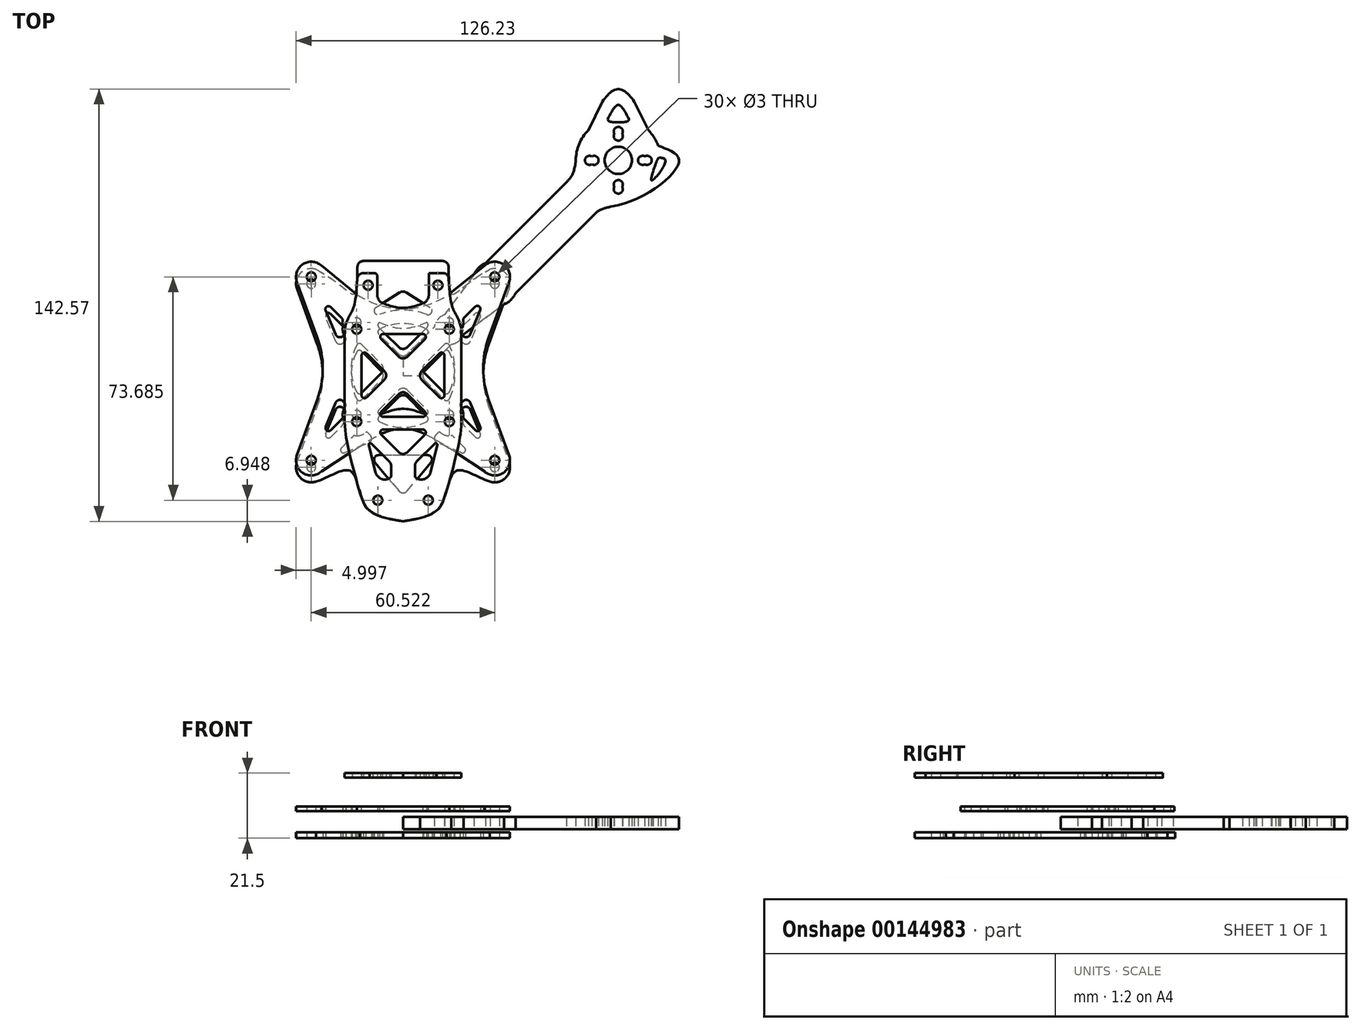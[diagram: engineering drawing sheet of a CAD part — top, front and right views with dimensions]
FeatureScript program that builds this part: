
annotation { "Feature Type Name" : "Feature", "Feature Type Description" : "" }
export const myFeature = defineFeature(function(context is Context, id is Id, definition is map)
    precondition{}
    {
        {
            var Q0;
            Q0=qCreatedBy(makeId("Top.planeOp"),FACE);
            var sketch = newSketch(context, id + "F0", { "sketchPlane" : qUnion([Q0])});
            skLineSegment(sketch, "E0.bottom", {"start": v(-15.25, 15.25) * mm, "end": v(15.25, 15.25) * mm, "construction": true});
            skLineSegment(sketch, "E0.top", {"start": v(-15.25, -15.25) * mm, "end": v(15.25, -15.25) * mm, "construction": true});
            skLineSegment(sketch, "E0.left", {"start": v(-15.25, 15.25) * mm, "end": v(-15.25, -15.25) * mm, "construction": true});
            skLineSegment(sketch, "E0.right", {"start": v(15.25, 15.25) * mm, "end": v(15.25, -15.25) * mm, "construction": true});
            skPoint(sketch, "E0.middle", {"position": v(0, 0) * mm});
            skLineSegment(sketch, "E1.bottom", {"start": v(30.25, 30.25) * mm, "end": v(-30.25, 30.25) * mm, "construction": true});
            skLineSegment(sketch, "E1.top", {"start": v(30.25, -30.25) * mm, "end": v(-30.25, -30.25) * mm, "construction": true});
            skLineSegment(sketch, "E1.left", {"start": v(30.25, 30.25) * mm, "end": v(30.25, -30.25) * mm, "construction": true});
            skLineSegment(sketch, "E1.right", {"start": v(-30.25, 30.25) * mm, "end": v(-30.25, -30.25) * mm, "construction": true});
            skLineSegment(sketch, "E2.bottom", {"start": v(-70.96, 70.96) * mm, "end": v(70.96, 70.96) * mm, "construction": true});
            skLineSegment(sketch, "E2.top", {"start": v(-70.96, -70.96) * mm, "end": v(70.96, -70.96) * mm, "construction": true});
            skLineSegment(sketch, "E2.left", {"start": v(-70.96, 70.96) * mm, "end": v(-70.96, -70.96) * mm, "construction": true});
            skLineSegment(sketch, "E2.right", {"start": v(70.96, 70.96) * mm, "end": v(70.96, -70.96) * mm, "construction": true});
            skCircle(sketch, "E3", {"center": v(70.96, 70.96) * mm, "radius": 8 * mm, "construction": true});
            skCircle(sketch, "E4", {"center": v(70.96, -70.96) * mm, "radius": 8 * mm, "construction": true});
            skCircle(sketch, "E5", {"center": v(-70.96, -70.96) * mm, "radius": 8 * mm, "construction": true});
            skCircle(sketch, "E6", {"center": v(-70.96, 70.96) * mm, "radius": 8 * mm, "construction": true});
            skCircle(sketch, "E7", {"center": v(70.96, 70.96) * mm, "radius": 9.5 * mm, "construction": true});
            skCircle(sketch, "E8", {"center": v(70.96, -70.96) * mm, "radius": 9.5 * mm, "construction": true});
            skCircle(sketch, "E9", {"center": v(-70.96, -70.96) * mm, "radius": 9.5 * mm, "construction": true});
            skCircle(sketch, "E10", {"center": v(-70.96, 70.96) * mm, "radius": 9.5 * mm, "construction": true});
            skCircle(sketch, "E11", {"center": v(70.96, 70.96) * mm, "radius": 14 * mm, "construction": true});
            skCircle(sketch, "E12", {"center": v(-70.96, 70.96) * mm, "radius": 14 * mm, "construction": true});
            skCircle(sketch, "E13", {"center": v(70.96, -70.96) * mm, "radius": 14 * mm, "construction": true});
            skCircle(sketch, "E14", {"center": v(-70.96, -70.96) * mm, "radius": 14 * mm, "construction": true});
            skCircle(sketch, "E15", {"center": v(70.96, 70.96) * mm, "radius": 63.5 * mm, "construction": true});
            skCircle(sketch, "E16", {"center": v(70.96, -70.96) * mm, "radius": 63.5 * mm, "construction": true});
            skCircle(sketch, "E17", {"center": v(-70.96, -70.96) * mm, "radius": 63.5 * mm, "construction": true});
            skCircle(sketch, "E18", {"center": v(-70.96, 70.96) * mm, "radius": 63.5 * mm, "construction": true});
            skLineSegment(sketch, "E19", {"start": v(0, 30.25) * mm, "end": v(0, 37.76) * mm, "construction": true});
            skLineSegment(sketch, "E20", {"start": v(0, 37.76) * mm, "end": v(-15, 37.76) * mm, "construction": true});
            skLineSegment(sketch, "E21", {"start": v(0, 37.76) * mm, "end": v(15, 37.76) * mm, "construction": true});
            skLineSegment(sketch, "E22", {"start": v(0, -30.25) * mm, "end": v(0, -37.76) * mm, "construction": true});
            skLineSegment(sketch, "E23.bottom", {"start": v(-26.17, 26.25) * mm, "end": v(26.21, 26.25) * mm, "construction": true});
            skLineSegment(sketch, "E23.top", {"start": v(-26.21, -26.25) * mm, "end": v(26.17, -26.25) * mm, "construction": true});
            skLineSegment(sketch, "E23.left", {"start": v(-26.17, 26.25) * mm, "end": v(-26.17, -26.13) * mm, "construction": true});
            skLineSegment(sketch, "E23.right", {"start": v(26.21, 26.25) * mm, "end": v(26.21, -26.2) * mm, "construction": true});
            skCircle(sketch, "E24", {"center": v(30.25, 30.25) * mm, "radius": 5 * mm, "construction": true});
            skCircle(sketch, "E25", {"center": v(-30.25, 30.25) * mm, "radius": 5 * mm, "construction": true});
            skCircle(sketch, "E26", {"center": v(30.25, -30.25) * mm, "radius": 5 * mm, "construction": true});
            skCircle(sketch, "E27", {"center": v(-30.25, -30.25) * mm, "radius": 5 * mm, "construction": true});
            skLineSegment(sketch, "E28.bottom", {"start": v(24.5, 24.5) * mm, "end": v(-24.5, 24.5) * mm, "construction": true});
            skLineSegment(sketch, "E28.top", {"start": v(24.5, -24.5) * mm, "end": v(-24.5, -24.5) * mm, "construction": true});
            skLineSegment(sketch, "E28.left", {"start": v(24.5, 24.5) * mm, "end": v(24.5, -24.5) * mm, "construction": true});
            skLineSegment(sketch, "E28.right", {"start": v(-24.5, 24.5) * mm, "end": v(-24.5, -24.5) * mm, "construction": true});
            skLineSegment(sketch, "E29", {"start": v(-26.17, 26.25) * mm, "end": v(-30.25, 30.25) * mm, "construction": true});
            skLineSegment(sketch, "E30", {"start": v(-26.68, 26.75) * mm, "end": v(-33.82, 33.75) * mm, "construction": true});
            skLineSegment(sketch, "E31", {"start": v(-31.8, 31.77) * mm, "end": v(-28.66, 34.99) * mm, "construction": true});
            skLineSegment(sketch, "E32", {"start": v(-31.8, 31.77) * mm, "end": v(-34.96, 28.56) * mm, "construction": true});
            skArc(sketch, "E33", {"start": v(-28.66, 34.99) * mm, "mid": v(-33.82, 33.75) * mm, "end": v(-34.96, 28.56) * mm});
            skLineSegment(sketch, "E34", {"start": v(26.21, 26.25) * mm, "end": v(30.25, 30.25) * mm, "construction": true});
            skLineSegment(sketch, "E35", {"start": v(26.7, 26.73) * mm, "end": v(33.8, 33.77) * mm, "construction": true});
            skLineSegment(sketch, "E36", {"start": v(31.8, 31.78) * mm, "end": v(34.96, 28.58) * mm, "construction": true});
            skLineSegment(sketch, "E37", {"start": v(31.8, 31.78) * mm, "end": v(28.63, 34.98) * mm, "construction": true});
            skArc(sketch, "E38", {"start": v(34.96, 28.58) * mm, "mid": v(33.8, 33.77) * mm, "end": v(28.63, 34.98) * mm});
            skLineSegment(sketch, "E39", {"start": v(26.17, -26.25) * mm, "end": v(30.25, -30.25) * mm, "construction": true});
            skLineSegment(sketch, "E40", {"start": v(26.68, -26.75) * mm, "end": v(33.82, -33.75) * mm, "construction": true});
            skLineSegment(sketch, "E41", {"start": v(31.8, -31.77) * mm, "end": v(34.96, -28.56) * mm, "construction": true});
            skLineSegment(sketch, "E42", {"start": v(31.8, -31.77) * mm, "end": v(28.66, -34.99) * mm, "construction": true});
            skArc(sketch, "E43", {"start": v(28.66, -34.99) * mm, "mid": v(33.82, -33.75) * mm, "end": v(34.96, -28.56) * mm});
            skLineSegment(sketch, "E44", {"start": v(-26.21, -26.25) * mm, "end": v(-30.25, -30.25) * mm, "construction": true});
            skLineSegment(sketch, "E45", {"start": v(-26.7, -26.73) * mm, "end": v(-33.8, -33.77) * mm, "construction": true});
            skLineSegment(sketch, "E46", {"start": v(-31.8, -31.78) * mm, "end": v(-28.63, -34.98) * mm, "construction": true});
            skLineSegment(sketch, "E47", {"start": v(-31.8, -31.78) * mm, "end": v(-34.96, -28.58) * mm, "construction": true});
            skArc(sketch, "E48", {"start": v(-34.96, -28.58) * mm, "mid": v(-33.8, -33.77) * mm, "end": v(-28.63, -34.98) * mm});
            skLineSegment(sketch, "E49", {"start": v(-34.96, -28.58) * mm, "end": v(-28.28, -10.31) * mm});
            skLineSegment(sketch, "E50", {"start": v(-28.28, 10.31) * mm, "end": v(-34.96, 28.56) * mm});
            skLineSegment(sketch, "E51", {"start": v(34.96, 28.58) * mm, "end": v(28.28, 10.31) * mm});
            skLineSegment(sketch, "E52", {"start": v(28.28, -10.31) * mm, "end": v(34.96, -28.56) * mm});
            skPoint(sketch, "E53.visualSharp", {"position": v(24.5, 0) * mm});
            skArc(sketch, "E53.filletArc", {"start": v(28.28, 10.31) * mm, "mid": v(26.45, 0) * mm, "end": v(28.28, -10.31) * mm});
            skPoint(sketch, "E54.visualSharp", {"position": v(-24.5, 0) * mm});
            skArc(sketch, "E54.filletArc", {"start": v(-28.28, -10.31) * mm, "mid": v(-26.45, 0) * mm, "end": v(-28.28, 10.31) * mm});
            skFitSpline(sketch, "E55", {"points": [v(-28.66, 34.99) * mm, v(-15, 37.76) * mm], "startDerivative": vector(40.9, -21.49) * mm, "endDerivative": vector(0.75, 54.16) * mm});
            skFitSpline(sketch, "E56", {"points": [v(15, 37.76) * mm, v(28.63, 34.98) * mm], "startDerivative": vector(0.75, -54.16) * mm, "endDerivative": vector(40.9, 21.46) * mm});
            skLineSegment(sketch, "E57", {"start": v(-15.25, 19.7) * mm, "end": v(15.25, 19.7) * mm, "construction": true});
            skPoint(sketch, "E58.endSnap0", {"position": v(0, -15.25) * mm});
            skLineSegment(sketch, "E59", {"start": v(-15.25, -19.7) * mm, "end": v(15.25, -19.7) * mm, "construction": true});
            skLineSegment(sketch, "E60", {"start": v(-14.33, -37.76) * mm, "end": v(14.33, -37.76) * mm, "construction": true});
            skLineSegment(sketch, "E61", {"start": v(-13.03, 37.76) * mm, "end": v(13.03, 37.76) * mm});
            skCircle(sketch, "E62", {"center": v(-30.25, 30.25) * mm, "radius": 1.5 * mm});
            skCircle(sketch, "E63", {"center": v(30.25, 30.25) * mm, "radius": 1.5 * mm});
            skCircle(sketch, "E64", {"center": v(15.25, 15.25) * mm, "radius": 1.5 * mm});
            skCircle(sketch, "E65", {"center": v(-15.25, 15.25) * mm, "radius": 1.5 * mm});
            skCircle(sketch, "E66", {"center": v(-15.25, -15.25) * mm, "radius": 1.5 * mm});
            skCircle(sketch, "E67", {"center": v(15.25, -15.25) * mm, "radius": 1.5 * mm});
            skCircle(sketch, "E68", {"center": v(30.25, -30.25) * mm, "radius": 1.5 * mm});
            skCircle(sketch, "E69", {"center": v(-30.25, -30.25) * mm, "radius": 1.5 * mm});
            skLineSegment(sketch, "E70", {"start": v(15, 37.76) * mm, "end": v(11.5, 37.76) * mm, "construction": true});
            skLineSegment(sketch, "E71", {"start": v(-15, 37.76) * mm, "end": v(-11.5, 37.76) * mm, "construction": true});
            skLineSegment(sketch, "E72", {"start": v(11.5, 37.76) * mm, "end": v(11.5, 29.76) * mm, "construction": true});
            skLineSegment(sketch, "E73", {"start": v(-11.5, 37.76) * mm, "end": v(-11.5, 29.76) * mm, "construction": true});
            skCircle(sketch, "E74", {"center": v(-11.5, 29.76) * mm, "radius": 1.5 * mm});
            skCircle(sketch, "E75", {"center": v(11.5, 29.76) * mm, "radius": 1.5 * mm});
            skLineSegment(sketch, "E76", {"start": v(0, 37.76) * mm, "end": v(0, 15.25) * mm, "construction": true});
            skLineSegment(sketch, "E77", {"start": v(0, -44.58) * mm, "end": v(-11, -44.58) * mm, "construction": true});
            skLineSegment(sketch, "E78", {"start": v(0, -44.58) * mm, "end": v(11, -44.58) * mm, "construction": true});
            skPoint(sketch, "E79.visualSharp", {"position": v(-14.33, -37.76) * mm});
            skPoint(sketch, "E80.visualSharp", {"position": v(14.33, -37.76) * mm});
            skCircle(sketch, "E81", {"center": v(0, 0) * mm, "radius": 17.11 * mm, "construction": true});
            skLineSegment(sketch, "E82", {"start": v(0, 0) * mm, "end": v(14.1, 14.1) * mm, "construction": true});
            skLineSegment(sketch, "E83", {"start": v(0, 0) * mm, "end": v(-15.25, 15.25) * mm, "construction": true});
            skLineSegment(sketch, "E84", {"start": v(0, 0) * mm, "end": v(-15.32, -15.32) * mm, "construction": true});
            skLineSegment(sketch, "E85", {"start": v(0, 0) * mm, "end": v(15.25, -15.25) * mm, "construction": true});
            skLineSegment(sketch, "E86", {"start": v(-10.7, 10.7) * mm, "end": v(-7.86, 13.52) * mm, "construction": true});
            skLineSegment(sketch, "E87", {"start": v(-10.7, 10.7) * mm, "end": v(-13.52, 7.86) * mm, "construction": true});
            skLineSegment(sketch, "E88", {"start": v(9.03, 9.03) * mm, "end": v(11.86, 6.2) * mm, "construction": true});
            skLineSegment(sketch, "E89", {"start": v(9.03, 9.03) * mm, "end": v(6.2, 11.86) * mm, "construction": true});
            skLineSegment(sketch, "E90", {"start": v(9.8, -9.8) * mm, "end": v(12.64, -6.98) * mm, "construction": true});
            skLineSegment(sketch, "E91", {"start": v(9.8, -9.8) * mm, "end": v(6.98, -12.64) * mm, "construction": true});
            skLineSegment(sketch, "E92", {"start": v(-9.52, -9.52) * mm, "end": v(-6.7, -12.35) * mm, "construction": true});
            skLineSegment(sketch, "E93", {"start": v(-9.52, -9.52) * mm, "end": v(-12.35, -6.7) * mm, "construction": true});
            skLineSegment(sketch, "E94.bottom", {"start": v(6.35, 6.35) * mm, "end": v(-6.35, 6.35) * mm, "construction": true});
            skLineSegment(sketch, "E94.top", {"start": v(6.35, -6.35) * mm, "end": v(-6.35, -6.35) * mm, "construction": true});
            skLineSegment(sketch, "E94.left", {"start": v(6.35, 6.35) * mm, "end": v(6.35, -6.35) * mm, "construction": true});
            skLineSegment(sketch, "E94.right", {"start": v(-6.35, 6.35) * mm, "end": v(-6.35, -6.35) * mm, "construction": true});
            skLineSegment(sketch, "E95", {"start": v(6.2, 11.86) * mm, "end": v(8.94, 14.6) * mm, "construction": true});
            skLineSegment(sketch, "E96", {"start": v(11.86, 6.2) * mm, "end": v(14.6, 8.94) * mm, "construction": true});
            skLineSegment(sketch, "E97", {"start": v(8, 13.66) * mm, "end": v(1.41, 7.07) * mm});
            skLineSegment(sketch, "E98", {"start": v(-1.41, 7.07) * mm, "end": v(-8, 13.66) * mm});
            skLineSegment(sketch, "E99", {"start": v(-13.52, 7.86) * mm, "end": v(-14.6, 8.94) * mm, "construction": true});
            skLineSegment(sketch, "E100", {"start": v(-6.7, -12.35) * mm, "end": v(-8.94, -14.6) * mm, "construction": true});
            skLineSegment(sketch, "E101", {"start": v(-8, -13.66) * mm, "end": v(-1.41, -7.07) * mm});
            skLineSegment(sketch, "E102", {"start": v(1.41, -7.07) * mm, "end": v(8, -13.66) * mm});
            skLineSegment(sketch, "E103", {"start": v(13.66, 8) * mm, "end": v(7.07, 1.41) * mm});
            skLineSegment(sketch, "E104", {"start": v(7.07, -1.41) * mm, "end": v(13.66, -8) * mm});
            skPoint(sketch, "E105", {"position": v(-7.77, 15.25) * mm});
            skPoint(sketch, "E106", {"position": v(7.77, 15.25) * mm});
            skPoint(sketch, "E107", {"position": v(15.25, 7.77) * mm});
            skPoint(sketch, "E108", {"position": v(15.25, -7.77) * mm});
            skPoint(sketch, "E109", {"position": v(7.77, -15.25) * mm});
            skPoint(sketch, "E110", {"position": v(-7.77, -15.25) * mm});
            skPoint(sketch, "E111", {"position": v(-15.25, -7.77) * mm});
            skPoint(sketch, "E112", {"position": v(-15.25, 7.77) * mm});
            skLineSegment(sketch, "E113", {"start": v(-7.79, 15.24) * mm, "end": v(-7.77, 15.25) * mm});
            skLineSegment(sketch, "E114", {"start": v(7.79, 15.24) * mm, "end": v(7.77, 15.25) * mm});
            skLineSegment(sketch, "E115", {"start": v(15.24, 7.79) * mm, "end": v(15.25, 7.77) * mm});
            skLineSegment(sketch, "E116", {"start": v(15.24, -7.79) * mm, "end": v(15.25, -7.77) * mm});
            skLineSegment(sketch, "E117", {"start": v(7.79, -15.24) * mm, "end": v(7.77, -15.25) * mm});
            skLineSegment(sketch, "E118", {"start": v(-7.77, -15.25) * mm, "end": v(-7.79, -15.24) * mm});
            skLineSegment(sketch, "E119", {"start": v(-15.24, -7.79) * mm, "end": v(-15.25, -7.77) * mm});
            skLineSegment(sketch, "E120", {"start": v(-15.24, 7.79) * mm, "end": v(-15.25, 7.77) * mm});
            skPoint(sketch, "E121", {"position": v(0, 17.11) * mm});
            skPoint(sketch, "E122", {"position": v(17.11, 0) * mm});
            skPoint(sketch, "E123", {"position": v(-17.11, 0) * mm});
            skPoint(sketch, "E124", {"position": v(0, -17.11) * mm});
            skArc(sketch, "E125", {"start": v(7.77, 15.25) * mm, "mid": v(0, 17.11) * mm, "end": v(-7.77, 15.25) * mm});
            skArc(sketch, "E126", {"start": v(15.25, -7.77) * mm, "mid": v(17.11, 0) * mm, "end": v(15.25, 7.77) * mm});
            skArc(sketch, "E127", {"start": v(-7.77, -15.25) * mm, "mid": v(0, -17.11) * mm, "end": v(7.77, -15.25) * mm});
            skArc(sketch, "E128", {"start": v(-15.25, 7.77) * mm, "mid": v(-17.11, 0) * mm, "end": v(-15.25, -7.77) * mm});
            skPoint(sketch, "E129.visualSharp", {"position": v(-5.66, 0) * mm});
            skPoint(sketch, "E130.visualSharp", {"position": v(-14.6, 8.94) * mm});
            skArc(sketch, "E130.filletArc", {"start": v(-13.66, 8) * mm, "mid": v(-14.5, 8.29) * mm, "end": v(-15.24, 7.79) * mm});
            skPoint(sketch, "E131.visualSharp", {"position": v(-14.6, -8.94) * mm});
            skArc(sketch, "E131.filletArc", {"start": v(-15.24, -7.79) * mm, "mid": v(-14.5, -8.29) * mm, "end": v(-13.66, -8) * mm});
            skPoint(sketch, "E132.visualSharp", {"position": v(-8.94, 14.6) * mm});
            skArc(sketch, "E132.filletArc", {"start": v(-7.79, 15.24) * mm, "mid": v(-8.29, 14.5) * mm, "end": v(-8, 13.66) * mm});
            skPoint(sketch, "E133.visualSharp", {"position": v(8.94, 14.6) * mm});
            skArc(sketch, "E133.filletArc", {"start": v(8, 13.66) * mm, "mid": v(8.29, 14.5) * mm, "end": v(7.79, 15.24) * mm});
            skPoint(sketch, "E134.visualSharp", {"position": v(14.6, -8.94) * mm});
            skArc(sketch, "E134.filletArc", {"start": v(13.66, -8) * mm, "mid": v(14.5, -8.29) * mm, "end": v(15.24, -7.79) * mm});
            skPoint(sketch, "E135.visualSharp", {"position": v(14.6, 8.94) * mm});
            skArc(sketch, "E135.filletArc", {"start": v(15.24, 7.79) * mm, "mid": v(14.5, 8.29) * mm, "end": v(13.66, 8) * mm});
            skPoint(sketch, "E136.visualSharp", {"position": v(8.94, -14.6) * mm});
            skArc(sketch, "E136.filletArc", {"start": v(7.79, -15.24) * mm, "mid": v(8.29, -14.5) * mm, "end": v(8, -13.66) * mm});
            skPoint(sketch, "E137.visualSharp", {"position": v(-8.94, -14.6) * mm});
            skArc(sketch, "E137.filletArc", {"start": v(-8, -13.66) * mm, "mid": v(-8.29, -14.5) * mm, "end": v(-7.79, -15.24) * mm});
            skLineSegment(sketch, "E138", {"start": v(-13.66, 8) * mm, "end": v(-7.07, 1.41) * mm});
            skLineSegment(sketch, "E139", {"start": v(-13.66, -8) * mm, "end": v(-7.07, -1.41) * mm});
            skArc(sketch, "E140.filletArc", {"start": v(-7.07, -1.41) * mm, "mid": v(-6.49, 0) * mm, "end": v(-7.07, 1.41) * mm});
            skPoint(sketch, "E141.visualSharp", {"position": v(0, -5.66) * mm});
            skArc(sketch, "E141.filletArc", {"start": v(1.41, -7.07) * mm, "mid": v(0, -6.49) * mm, "end": v(-1.41, -7.07) * mm});
            skPoint(sketch, "E142.visualSharp", {"position": v(5.66, 0) * mm});
            skArc(sketch, "E142.filletArc", {"start": v(7.07, 1.41) * mm, "mid": v(6.49, 0) * mm, "end": v(7.07, -1.41) * mm});
            skPoint(sketch, "E143.visualSharp", {"position": v(0, 5.66) * mm});
            skArc(sketch, "E143.filletArc", {"start": v(-1.41, 7.07) * mm, "mid": v(0, 6.49) * mm, "end": v(1.41, 7.07) * mm});
            skLineSegment(sketch, "E144", {"start": v(-12.9, 12.9) * mm, "end": v(-11.14, 14.67) * mm, "construction": true});
            skLineSegment(sketch, "E145", {"start": v(-12.9, 12.9) * mm, "end": v(-14.67, 11.14) * mm, "construction": true});
            skLineSegment(sketch, "E146", {"start": v(-14.67, 11.14) * mm, "end": v(-27.4, 23.87) * mm, "construction": true});
            skPoint(sketch, "E147", {"position": v(-17.57, 14.03) * mm});
            skCircle(sketch, "E148", {"center": v(-15.25, 15.25) * mm, "radius": 4.62 * mm, "construction": true});
            skLineSegment(sketch, "E149", {"start": v(-27.4, 23.87) * mm, "end": v(-21.1, 8.64) * mm, "construction": true});
            skLineSegment(sketch, "E150", {"start": v(-15.25, 15.25) * mm, "end": v(-21.32, 9.18) * mm, "construction": true});
            skLineSegment(sketch, "E151", {"start": v(-18.86, 11.64) * mm, "end": v(-19.74, 10.76) * mm});
            skLineSegment(sketch, "E152", {"start": v(-22.18, 11.25) * mm, "end": v(-25.48, 19.23) * mm});
            skLineSegment(sketch, "E153", {"start": v(-23.85, 20.32) * mm, "end": v(-20.04, 16.5) * mm});
            skLineSegment(sketch, "E154", {"start": v(-19.83, 15.85) * mm, "end": v(-19.85, 15.74) * mm});
            skLineSegment(sketch, "E155", {"start": v(-18.84, 12.33) * mm, "end": v(-18.85, 12.35) * mm});
            skPoint(sketch, "E156", {"position": v(-19.67, 13.9) * mm});
            skArc(sketch, "E157", {"start": v(-19.85, 15.74) * mm, "mid": v(-19.69, 13.95) * mm, "end": v(-18.85, 12.35) * mm});
            skPoint(sketch, "E158.visualSharp", {"position": v(-27.4, 23.87) * mm});
            skArc(sketch, "E158.filletArc", {"start": v(-23.85, 20.32) * mm, "mid": v(-25.11, 20.44) * mm, "end": v(-25.48, 19.23) * mm});
            skPoint(sketch, "E159.visualSharp", {"position": v(-21.32, 9.18) * mm});
            skArc(sketch, "E159.filletArc", {"start": v(-22.18, 11.25) * mm, "mid": v(-21.1, 10.35) * mm, "end": v(-19.74, 10.76) * mm});
            skPoint(sketch, "E160.visualSharp", {"position": v(-18.52, 11.98) * mm});
            skArc(sketch, "E160.filletArc", {"start": v(-18.86, 11.64) * mm, "mid": v(-18.7, 11.98) * mm, "end": v(-18.84, 12.33) * mm});
            skPoint(sketch, "E161.visualSharp", {"position": v(-19.77, 16.23) * mm});
            skArc(sketch, "E161.filletArc", {"start": v(-19.83, 15.85) * mm, "mid": v(-19.86, 16.2) * mm, "end": v(-20.04, 16.5) * mm});
            skCircle(sketch, "E162", {"center": v(15.23, 15.26) * mm, "radius": 4.62 * mm, "construction": true});
            skLineSegment(sketch, "E163", {"start": v(15.23, 15.26) * mm, "end": v(12.9, 12.9) * mm, "construction": true});
            skLineSegment(sketch, "E164", {"start": v(12.9, 12.9) * mm, "end": v(14.68, 11.15) * mm, "construction": true});
            skLineSegment(sketch, "E165", {"start": v(12.9, 12.9) * mm, "end": v(11.12, 14.66) * mm, "construction": true});
            skLineSegment(sketch, "E166", {"start": v(11.12, 14.66) * mm, "end": v(23.85, 27.39) * mm, "construction": true});
            skLineSegment(sketch, "E167", {"start": v(14.68, 11.15) * mm, "end": v(27.32, 23.97) * mm, "construction": true});
            skLineSegment(sketch, "E168", {"start": v(15.25, 15.25) * mm, "end": v(21.37, 9.22) * mm, "construction": true});
            skLineSegment(sketch, "E169", {"start": v(21.37, 9.22) * mm, "end": v(27.32, 23.97) * mm, "construction": true});
            skLineSegment(sketch, "E170", {"start": v(19.8, 15.9) * mm, "end": v(19.82, 15.79) * mm});
            skLineSegment(sketch, "E171", {"start": v(18.84, 12.37) * mm, "end": v(18.86, 12.4) * mm});
            skLineSegment(sketch, "E172", {"start": v(20.01, 16.55) * mm, "end": v(23.8, 20.4) * mm});
            skLineSegment(sketch, "E173", {"start": v(25.45, 19.33) * mm, "end": v(22.2, 11.3) * mm});
            skLineSegment(sketch, "E174", {"start": v(19.77, 10.8) * mm, "end": v(18.86, 11.69) * mm});
            skPoint(sketch, "E175", {"position": v(19.65, 13.92) * mm});
            skArc(sketch, "E176", {"start": v(18.86, 12.4) * mm, "mid": v(19.68, 14) * mm, "end": v(19.82, 15.79) * mm});
            skPoint(sketch, "E177.visualSharp", {"position": v(18.53, 12.02) * mm});
            skArc(sketch, "E177.filletArc", {"start": v(18.84, 12.37) * mm, "mid": v(18.72, 12.03) * mm, "end": v(18.86, 11.69) * mm});
            skPoint(sketch, "E178.visualSharp", {"position": v(19.74, 16.28) * mm});
            skArc(sketch, "E178.filletArc", {"start": v(20.01, 16.55) * mm, "mid": v(19.83, 16.25) * mm, "end": v(19.8, 15.9) * mm});
            skPoint(sketch, "E179.visualSharp", {"position": v(27.32, 23.97) * mm});
            skArc(sketch, "E179.filletArc", {"start": v(25.45, 19.33) * mm, "mid": v(25.07, 20.54) * mm, "end": v(23.8, 20.4) * mm});
            skPoint(sketch, "E180.visualSharp", {"position": v(21.37, 9.22) * mm});
            skArc(sketch, "E180.filletArc", {"start": v(19.77, 10.8) * mm, "mid": v(21.12, 10.4) * mm, "end": v(22.2, 11.3) * mm});
            skCircle(sketch, "E181", {"center": v(-15.25, -15.25) * mm, "radius": 4.62 * mm, "construction": true});
            skCircle(sketch, "E182", {"center": v(15.25, -15.25) * mm, "radius": 4.62 * mm, "construction": true});
            skLineSegment(sketch, "E183", {"start": v(-15.25, -15.25) * mm, "end": v(-12.9, -12.9) * mm, "construction": true});
            skLineSegment(sketch, "E184", {"start": v(-12.9, -12.9) * mm, "end": v(-11.14, -14.67) * mm, "construction": true});
            skLineSegment(sketch, "E185", {"start": v(-12.9, -12.9) * mm, "end": v(-14.67, -11.14) * mm, "construction": true});
            skLineSegment(sketch, "E186", {"start": v(-11.14, -14.67) * mm, "end": v(-23.87, -27.4) * mm, "construction": true});
            skLineSegment(sketch, "E187", {"start": v(-14.67, -11.14) * mm, "end": v(-27.4, -23.87) * mm, "construction": true});
            skLineSegment(sketch, "E188", {"start": v(-15.25, -15.25) * mm, "end": v(-9.18, -21.32) * mm, "construction": true});
            skLineSegment(sketch, "E189", {"start": v(-15.25, -15.25) * mm, "end": v(-21.32, -9.18) * mm, "construction": true});
            skLineSegment(sketch, "E190", {"start": v(-25.48, -19.23) * mm, "end": v(-22.18, -11.25) * mm});
            skLineSegment(sketch, "E191", {"start": v(-19.74, -10.76) * mm, "end": v(-18.86, -11.64) * mm});
            skLineSegment(sketch, "E192", {"start": v(-23.85, -20.32) * mm, "end": v(-20.04, -16.5) * mm});
            skLineSegment(sketch, "E193", {"start": v(-18.84, -12.33) * mm, "end": v(-18.85, -12.35) * mm});
            skLineSegment(sketch, "E194", {"start": v(-19.83, -15.85) * mm, "end": v(-19.85, -15.74) * mm});
            skPoint(sketch, "E195", {"position": v(-19.69, -13.94) * mm});
            skArc(sketch, "E196", {"start": v(-18.85, -12.35) * mm, "mid": v(-19.69, -13.95) * mm, "end": v(-19.85, -15.74) * mm});
            skPoint(sketch, "E197.visualSharp", {"position": v(-18.52, -11.98) * mm});
            skArc(sketch, "E197.filletArc", {"start": v(-18.84, -12.33) * mm, "mid": v(-18.7, -11.98) * mm, "end": v(-18.86, -11.64) * mm});
            skPoint(sketch, "E198.visualSharp", {"position": v(-19.77, -16.23) * mm});
            skArc(sketch, "E198.filletArc", {"start": v(-20.04, -16.5) * mm, "mid": v(-19.86, -16.2) * mm, "end": v(-19.83, -15.85) * mm});
            skPoint(sketch, "E199.visualSharp", {"position": v(-27.4, -23.87) * mm});
            skArc(sketch, "E199.filletArc", {"start": v(-25.48, -19.23) * mm, "mid": v(-25.11, -20.44) * mm, "end": v(-23.85, -20.32) * mm});
            skPoint(sketch, "E200.visualSharp", {"position": v(-21.32, -9.18) * mm});
            skArc(sketch, "E200.filletArc", {"start": v(-19.74, -10.76) * mm, "mid": v(-21.1, -10.35) * mm, "end": v(-22.18, -11.25) * mm});
            skLineSegment(sketch, "E201", {"start": v(15.25, -15.25) * mm, "end": v(12.9, -12.9) * mm, "construction": true});
            skLineSegment(sketch, "E202", {"start": v(12.9, -12.9) * mm, "end": v(14.67, -11.14) * mm, "construction": true});
            skLineSegment(sketch, "E203", {"start": v(12.9, -12.9) * mm, "end": v(11.14, -14.67) * mm, "construction": true});
            skLineSegment(sketch, "E204", {"start": v(14.67, -11.14) * mm, "end": v(27.4, -23.87) * mm, "construction": true});
            skLineSegment(sketch, "E205", {"start": v(15.25, -15.25) * mm, "end": v(21.32, -9.18) * mm, "construction": true});
            skLineSegment(sketch, "E206", {"start": v(22.18, -11.25) * mm, "end": v(25.48, -19.23) * mm});
            skLineSegment(sketch, "E207", {"start": v(23.85, -20.32) * mm, "end": v(20.04, -16.5) * mm});
            skLineSegment(sketch, "E208", {"start": v(19.74, -10.76) * mm, "end": v(18.86, -11.64) * mm});
            skLineSegment(sketch, "E209", {"start": v(18.84, -12.33) * mm, "end": v(18.85, -12.35) * mm});
            skLineSegment(sketch, "E210", {"start": v(19.83, -15.85) * mm, "end": v(19.85, -15.74) * mm});
            skPoint(sketch, "E211", {"position": v(19.64, -13.8) * mm});
            skArc(sketch, "E212", {"start": v(19.85, -15.74) * mm, "mid": v(19.69, -13.95) * mm, "end": v(18.85, -12.35) * mm});
            skPoint(sketch, "E213.visualSharp", {"position": v(21.32, -9.18) * mm});
            skArc(sketch, "E213.filletArc", {"start": v(22.18, -11.25) * mm, "mid": v(21.1, -10.35) * mm, "end": v(19.74, -10.76) * mm});
            skPoint(sketch, "E214.visualSharp", {"position": v(19.77, -16.23) * mm});
            skArc(sketch, "E214.filletArc", {"start": v(19.83, -15.85) * mm, "mid": v(19.86, -16.2) * mm, "end": v(20.04, -16.5) * mm});
            skPoint(sketch, "E215.visualSharp", {"position": v(18.52, -11.98) * mm});
            skArc(sketch, "E215.filletArc", {"start": v(18.86, -11.64) * mm, "mid": v(18.7, -11.98) * mm, "end": v(18.84, -12.33) * mm});
            skPoint(sketch, "E216.visualSharp", {"position": v(27.4, -23.87) * mm});
            skArc(sketch, "E216.filletArc", {"start": v(23.85, -20.32) * mm, "mid": v(25.11, -20.44) * mm, "end": v(25.48, -19.23) * mm});
            skPoint(sketch, "E217", {"position": v(0, -48.1) * mm});
            skLineSegment(sketch, "E218", {"start": v(0, -31.42) * mm, "end": v(17.54, -31.42) * mm, "construction": true});
            skLineSegment(sketch, "E219", {"start": v(0, -31.42) * mm, "end": v(-17.54, -31.42) * mm, "construction": true});
            skFitSpline(sketch, "E220", {"points": [v(28.66, -34.99) * mm, v(17.54, -31.42) * mm, v(14.33, -37.76) * mm], "startDerivative": vector(-22.15, 6.9) * mm, "endDerivative": vector(-5.52, -13.66) * mm});
            skFitSpline(sketch, "E221", {"points": [v(14.33, -37.76) * mm, v(11, -44.58) * mm, v(0, -48.1) * mm], "startDerivative": vector(-4.65, -17.21) * mm, "endDerivative": vector(-23.36, -3.95) * mm});
            skFitSpline(sketch, "E222", {"points": [v(-28.63, -34.98) * mm, v(-17.54, -31.42) * mm, v(-14.33, -37.76) * mm], "startDerivative": vector(22.11, 6.89) * mm, "endDerivative": vector(5.52, -13.65) * mm});
            skFitSpline(sketch, "E223", {"points": [v(-14.33, -37.76) * mm, v(-11, -44.58) * mm, v(0, -48.1) * mm], "startDerivative": vector(4.65, -17.21) * mm, "endDerivative": vector(23.36, -3.95) * mm});
            skLineSegment(sketch, "E224", {"start": v(-19.23, -25.48) * mm, "end": v(-11.25, -22.18) * mm});
            skLineSegment(sketch, "E225", {"start": v(-10.76, -19.74) * mm, "end": v(-11.64, -18.86) * mm});
            skLineSegment(sketch, "E226", {"start": v(-12.33, -18.84) * mm, "end": v(-12.35, -18.85) * mm});
            skLineSegment(sketch, "E227", {"start": v(-20.32, -23.85) * mm, "end": v(-16.5, -20.04) * mm});
            skLineSegment(sketch, "E228", {"start": v(-15.85, -19.83) * mm, "end": v(-15.74, -19.85) * mm});
            skPoint(sketch, "E229.visualSharp", {"position": v(-9.18, -21.32) * mm});
            skArc(sketch, "E229.filletArc", {"start": v(-11.25, -22.18) * mm, "mid": v(-10.35, -21.1) * mm, "end": v(-10.76, -19.74) * mm});
            skPoint(sketch, "E230.visualSharp", {"position": v(-11.98, -18.52) * mm});
            skArc(sketch, "E230.filletArc", {"start": v(-11.64, -18.86) * mm, "mid": v(-11.98, -18.7) * mm, "end": v(-12.33, -18.84) * mm});
            skPoint(sketch, "E231.visualSharp", {"position": v(-16.23, -19.77) * mm});
            skArc(sketch, "E231.filletArc", {"start": v(-15.85, -19.83) * mm, "mid": v(-16.2, -19.86) * mm, "end": v(-16.5, -20.04) * mm});
            skPoint(sketch, "E232.visualSharp", {"position": v(-23.87, -27.4) * mm});
            skArc(sketch, "E232.filletArc", {"start": v(-20.32, -23.85) * mm, "mid": v(-20.44, -25.11) * mm, "end": v(-19.23, -25.48) * mm});
            skLineSegment(sketch, "E233", {"start": v(15.25, -15.25) * mm, "end": v(9.18, -21.32) * mm, "construction": true});
            skLineSegment(sketch, "E234", {"start": v(11.14, -14.67) * mm, "end": v(23.87, -27.4) * mm, "construction": true});
            skLineSegment(sketch, "E235", {"start": v(19.23, -25.48) * mm, "end": v(11.25, -22.18) * mm});
            skLineSegment(sketch, "E236", {"start": v(10.76, -19.74) * mm, "end": v(11.64, -18.86) * mm});
            skLineSegment(sketch, "E237", {"start": v(12.33, -18.84) * mm, "end": v(12.35, -18.85) * mm});
            skLineSegment(sketch, "E238", {"start": v(20.32, -23.85) * mm, "end": v(16.5, -20.04) * mm});
            skLineSegment(sketch, "E239", {"start": v(15.85, -19.83) * mm, "end": v(15.74, -19.85) * mm});
            skPoint(sketch, "E240", {"position": v(13.76, -19.63) * mm});
            skArc(sketch, "E241", {"start": v(12.35, -18.85) * mm, "mid": v(13.95, -19.69) * mm, "end": v(15.74, -19.85) * mm});
            skPoint(sketch, "E242.visualSharp", {"position": v(9.18, -21.32) * mm});
            skArc(sketch, "E242.filletArc", {"start": v(10.76, -19.74) * mm, "mid": v(10.35, -21.1) * mm, "end": v(11.25, -22.18) * mm});
            skPoint(sketch, "E243.visualSharp", {"position": v(11.98, -18.52) * mm});
            skArc(sketch, "E243.filletArc", {"start": v(12.33, -18.84) * mm, "mid": v(11.98, -18.7) * mm, "end": v(11.64, -18.86) * mm});
            skPoint(sketch, "E244.visualSharp", {"position": v(23.87, -27.4) * mm});
            skArc(sketch, "E244.filletArc", {"start": v(19.23, -25.48) * mm, "mid": v(20.44, -25.11) * mm, "end": v(20.32, -23.85) * mm});
            skPoint(sketch, "E245.visualSharp", {"position": v(16.23, -19.77) * mm});
            skArc(sketch, "E245.filletArc", {"start": v(16.5, -20.04) * mm, "mid": v(16.2, -19.86) * mm, "end": v(15.85, -19.83) * mm});
            skPoint(sketch, "E246", {"position": v(-14.29, -19.77) * mm});
            skArc(sketch, "E247", {"start": v(-15.74, -19.85) * mm, "mid": v(-13.95, -19.69) * mm, "end": v(-12.35, -18.85) * mm});
            skArc(sketch, "E248.filletArc", {"start": v(-13.03, 37.76) * mm, "mid": v(-14.43, 37.18) * mm, "end": v(-15.03, 35.79) * mm});
            skArc(sketch, "E249.filletArc", {"start": v(15.03, 35.79) * mm, "mid": v(14.43, 37.18) * mm, "end": v(13.03, 37.76) * mm});
            skLineSegment(sketch, "E250", {"start": v(-13.27, -41.16) * mm, "end": v(-8.27, -41.16) * mm, "construction": true});
            skLineSegment(sketch, "E251", {"start": v(-8.27, -41.16) * mm, "end": v(-8.27, -46.16) * mm, "construction": true});
            skLineSegment(sketch, "E252", {"start": v(13.27, -41.16) * mm, "end": v(8.27, -41.16) * mm, "construction": true});
            skLineSegment(sketch, "E253", {"start": v(8.27, -41.16) * mm, "end": v(8.27, -46.16) * mm, "construction": true});
            skCircle(sketch, "E254", {"center": v(8.27, -41.16) * mm, "radius": 1.5 * mm});
            skCircle(sketch, "E255", {"center": v(-8.27, -41.16) * mm, "radius": 1.5 * mm});
            skLineSegment(sketch, "E256", {"start": v(-8.94, 14.6) * mm, "end": v(-8.94, 19.63) * mm, "construction": true});
            skLineSegment(sketch, "E257", {"start": v(8.94, 14.6) * mm, "end": v(8.94, 19.63) * mm, "construction": true});
            skPoint(sketch, "E258", {"position": v(0, 21.57) * mm});
            skLineSegment(sketch, "E259", {"start": v(-7.77, 15.25) * mm, "end": v(-7.77, 20.12) * mm, "construction": true});
            skLineSegment(sketch, "E260", {"start": v(7.79, 15.24) * mm, "end": v(7.79, 20.11) * mm, "construction": true});
            skLineSegment(sketch, "E261", {"start": v(-8.94, 19.63) * mm, "end": v(-8.94, 22.43) * mm, "construction": true});
            skLineSegment(sketch, "E262", {"start": v(8.94, 19.63) * mm, "end": v(8.94, 22.43) * mm, "construction": true});
            skLineSegment(sketch, "E263", {"start": v(-8.94, 22.43) * mm, "end": v(-1.06, 27.36) * mm});
            skLineSegment(sketch, "E264", {"start": v(1.06, 27.36) * mm, "end": v(8.94, 22.43) * mm});
            skArc(sketch, "E265", {"start": v(-8.94, 22.43) * mm, "mid": v(-9.4, 20.74) * mm, "end": v(-7.77, 20.12) * mm});
            skArc(sketch, "E266", {"start": v(7.79, 20.11) * mm, "mid": v(9.41, 20.75) * mm, "end": v(8.94, 22.43) * mm});
            skPoint(sketch, "E267.visualSharp", {"position": v(0, 28.02) * mm});
            skArc(sketch, "E267.filletArc", {"start": v(1.06, 27.36) * mm, "mid": v(0, 27.66) * mm, "end": v(-1.06, 27.36) * mm});
            skArc(sketch, "E268", {"start": v(7.79, 20.11) * mm, "mid": v(0, 21.57) * mm, "end": v(-7.77, 20.12) * mm});
            skLineSegment(sketch, "E269", {"start": v(-8.94, -14.6) * mm, "end": v(-8.94, -19.63) * mm, "construction": true});
            skLineSegment(sketch, "E270", {"start": v(-7.77, -15.25) * mm, "end": v(-7.77, -20.12) * mm, "construction": true});
            skLineSegment(sketch, "E271", {"start": v(7.79, -15.24) * mm, "end": v(7.79, -20.11) * mm, "construction": true});
            skLineSegment(sketch, "E272", {"start": v(8.94, -14.6) * mm, "end": v(8.94, -19.63) * mm, "construction": true});
            skLineSegment(sketch, "E273", {"start": v(-8.94, -19.63) * mm, "end": v(-8.94, -22.43) * mm, "construction": true});
            skLineSegment(sketch, "E274", {"start": v(8.94, -19.63) * mm, "end": v(8.94, -22.43) * mm, "construction": true});
            skPoint(sketch, "E275", {"position": v(0, -26.25) * mm});
            skPoint(sketch, "E276.visualSharp", {"position": v(0, -30.25) * mm});
            skPoint(sketch, "E277", {"position": v(0, -24.5) * mm});
            skLineSegment(sketch, "E278", {"start": v(0, -26.25) * mm, "end": v(-11.25, -26.25) * mm, "construction": true});
            skLineSegment(sketch, "E279", {"start": v(0, -26.25) * mm, "end": v(11.25, -26.25) * mm, "construction": true});
            skPoint(sketch, "E280.visualSharp", {"position": v(-11.25, -26.25) * mm});
            skPoint(sketch, "E281.visualSharp", {"position": v(11.25, -26.25) * mm});
            skPoint(sketch, "E282.visualSharp", {"position": v(0, -37.76) * mm});
            skPoint(sketch, "E283", {"position": v(0, -39.7) * mm});
            skLineSegment(sketch, "E284", {"start": v(-9.19, -28.72) * mm, "end": v(-1.34, -38.1) * mm});
            skLineSegment(sketch, "E285", {"start": v(1.34, -38.1) * mm, "end": v(9.19, -28.72) * mm});
            skLineSegment(sketch, "E286", {"start": v(-8.04, -26.25) * mm, "end": v(8.04, -26.25) * mm});
            skArc(sketch, "E287.filletArc", {"start": v(-8.04, -26.25) * mm, "mid": v(-9.4, -27.12) * mm, "end": v(-9.19, -28.72) * mm});
            skArc(sketch, "E288.filletArc", {"start": v(9.19, -28.72) * mm, "mid": v(9.4, -27.12) * mm, "end": v(8.04, -26.25) * mm});
            skArc(sketch, "E289.filletArc", {"start": v(-1.34, -38.1) * mm, "mid": v(0, -38.72) * mm, "end": v(1.34, -38.1) * mm});
            skLineSegment(sketch, "E290", {"start": v(0, 34) * mm, "end": v(8.73, 34) * mm, "construction": true});
            skLineSegment(sketch, "E291", {"start": v(0, 34) * mm, "end": v(-8.73, 34) * mm, "construction": true});
            skLineSegment(sketch, "E292", {"start": v(11.5, 31.26) * mm, "end": v(0, 31.26) * mm, "construction": true});
            skLineSegment(sketch, "E293", {"start": v(0, 31.26) * mm, "end": v(0, 50.76) * mm, "construction": true});
            skLineSegment(sketch, "E294", {"start": v(0, 50.76) * mm, "end": v(0, 63.06) * mm, "construction": true});
            skLineSegment(sketch, "E295", {"start": v(0, 63.06) * mm, "end": v(6.75, 63.06) * mm, "construction": true});
            skSolve(sketch);
        }
        {
            var Q0;
            Q0=qCreatedBy(makeId("Top.planeOp"),FACE);
            var sketch = newSketch(context, id + "F1", { "sketchPlane" : qUnion([Q0])});
            skLineSegment(sketch, "E296.bottom", {"start": v(-15.24, 15.25) * mm, "end": v(15.26, 15.25) * mm, "construction": true});
            skLineSegment(sketch, "E296.top", {"start": v(-15.24, -15.25) * mm, "end": v(15.26, -15.25) * mm, "construction": true});
            skLineSegment(sketch, "E296.left", {"start": v(-15.24, 15.25) * mm, "end": v(-15.24, -15.25) * mm, "construction": true});
            skLineSegment(sketch, "E296.right", {"start": v(15.26, 15.25) * mm, "end": v(15.26, -15.25) * mm, "construction": true});
            skPoint(sketch, "E296.middle", {"position": v(0, 0) * mm});
            skLineSegment(sketch, "E297.bottom", {"start": v(30.26, 30.25) * mm, "end": v(-30.24, 30.25) * mm, "construction": true});
            skLineSegment(sketch, "E297.top", {"start": v(30.26, -30.25) * mm, "end": v(-30.24, -30.25) * mm, "construction": true});
            skLineSegment(sketch, "E297.left", {"start": v(30.26, 30.25) * mm, "end": v(30.26, -30.25) * mm, "construction": true});
            skLineSegment(sketch, "E297.right", {"start": v(-30.24, 30.25) * mm, "end": v(-30.24, -30.25) * mm, "construction": true});
            skLineSegment(sketch, "E298.bottom", {"start": v(-70.95, 70.96) * mm, "end": v(70.97, 70.96) * mm, "construction": true});
            skLineSegment(sketch, "E298.top", {"start": v(-70.95, -70.96) * mm, "end": v(70.97, -70.96) * mm, "construction": true});
            skLineSegment(sketch, "E298.left", {"start": v(-70.95, 70.96) * mm, "end": v(-70.95, -70.96) * mm, "construction": true});
            skLineSegment(sketch, "E298.right", {"start": v(70.97, 70.96) * mm, "end": v(70.97, -70.96) * mm, "construction": true});
            skCircle(sketch, "E299", {"center": v(70.97, 70.96) * mm, "radius": 4.5 * mm});
            skCircle(sketch, "E300", {"center": v(-70.95, 70.96) * mm, "radius": 4.5 * mm, "construction": true});
            skCircle(sketch, "E301", {"center": v(70.97, -70.96) * mm, "radius": 4.5 * mm, "construction": true});
            skCircle(sketch, "E302", {"center": v(-70.95, -70.96) * mm, "radius": 4.5 * mm, "construction": true});
            skCircle(sketch, "E303", {"center": v(70.97, 70.96) * mm, "radius": 8 * mm, "construction": true});
            skCircle(sketch, "E304", {"center": v(70.97, -70.96) * mm, "radius": 8 * mm, "construction": true});
            skCircle(sketch, "E305", {"center": v(-70.95, -70.96) * mm, "radius": 8 * mm, "construction": true});
            skCircle(sketch, "E306", {"center": v(-70.95, 70.96) * mm, "radius": 8 * mm, "construction": true});
            skCircle(sketch, "E307", {"center": v(70.97, 70.96) * mm, "radius": 9.5 * mm, "construction": true});
            skCircle(sketch, "E308", {"center": v(70.97, -70.96) * mm, "radius": 9.5 * mm, "construction": true});
            skCircle(sketch, "E309", {"center": v(-70.95, -70.96) * mm, "radius": 9.5 * mm, "construction": true});
            skCircle(sketch, "E310", {"center": v(-70.95, 70.96) * mm, "radius": 9.5 * mm, "construction": true});
            skCircle(sketch, "E311", {"center": v(70.97, 70.96) * mm, "radius": 14 * mm, "construction": true});
            skCircle(sketch, "E312", {"center": v(-70.95, 70.96) * mm, "radius": 14 * mm, "construction": true});
            skCircle(sketch, "E313", {"center": v(70.97, -70.96) * mm, "radius": 14 * mm, "construction": true});
            skCircle(sketch, "E314", {"center": v(-70.95, -70.96) * mm, "radius": 14 * mm, "construction": true});
            skCircle(sketch, "E315", {"center": v(70.97, 70.96) * mm, "radius": 63.5 * mm, "construction": true});
            skCircle(sketch, "E316", {"center": v(70.97, -70.96) * mm, "radius": 63.5 * mm, "construction": true});
            skCircle(sketch, "E317", {"center": v(-70.95, -70.96) * mm, "radius": 63.5 * mm, "construction": true});
            skCircle(sketch, "E318", {"center": v(-70.95, 70.96) * mm, "radius": 63.5 * mm, "construction": true});
            skLineSegment(sketch, "E319", {"start": v(0, 30.25) * mm, "end": v(0, 36.4) * mm, "construction": true});
            skLineSegment(sketch, "E320", {"start": v(0, 36.4) * mm, "end": v(-14.28, 36.4) * mm, "construction": true});
            skLineSegment(sketch, "E321", {"start": v(0, 36.4) * mm, "end": v(14.3, 36.4) * mm, "construction": true});
            skLineSegment(sketch, "E322", {"start": v(0, -30.25) * mm, "end": v(0, -36.4) * mm, "construction": true});
            skLineSegment(sketch, "E323", {"start": v(0, -36.4) * mm, "end": v(-14.28, -36.4) * mm, "construction": true});
            skLineSegment(sketch, "E324", {"start": v(0, -36.4) * mm, "end": v(14.3, -36.4) * mm, "construction": true});
            skLineSegment(sketch, "E325.bottom", {"start": v(-26.18, 26.2) * mm, "end": v(26.2, 26.2) * mm, "construction": true});
            skLineSegment(sketch, "E325.top", {"start": v(-26.18, -26.19) * mm, "end": v(26.2, -26.19) * mm, "construction": true});
            skLineSegment(sketch, "E325.left", {"start": v(-26.18, 26.2) * mm, "end": v(-26.18, -26.19) * mm, "construction": true});
            skLineSegment(sketch, "E325.right", {"start": v(26.2, 26.2) * mm, "end": v(26.2, -26.19) * mm, "construction": true});
            skCircle(sketch, "E326", {"center": v(30.26, 30.25) * mm, "radius": 7.5 * mm, "construction": true});
            skCircle(sketch, "E327", {"center": v(-30.24, 30.25) * mm, "radius": 7.5 * mm, "construction": true});
            skCircle(sketch, "E328", {"center": v(30.26, -30.25) * mm, "radius": 7.5 * mm, "construction": true});
            skCircle(sketch, "E329", {"center": v(-30.24, -30.25) * mm, "radius": 7.5 * mm, "construction": true});
            skCircle(sketch, "E330", {"center": v(15.26, 15.25) * mm, "radius": 1.5 * mm, "construction": true});
            skCircle(sketch, "E331", {"center": v(-15.24, 15.25) * mm, "radius": 1.5 * mm, "construction": true});
            skCircle(sketch, "E332", {"center": v(15.26, -15.25) * mm, "radius": 1.5 * mm, "construction": true});
            skCircle(sketch, "E333", {"center": v(-15.24, -15.25) * mm, "radius": 1.5 * mm, "construction": true});
            skLineSegment(sketch, "E334", {"start": v(15.26, 15.25) * mm, "end": v(0, 0) * mm, "construction": true});
            skLineSegment(sketch, "E335", {"start": v(-15.24, 15.25) * mm, "end": v(0, 0) * mm, "construction": true});
            skLineSegment(sketch, "E336", {"start": v(15.26, -15.25) * mm, "end": v(0, 0) * mm, "construction": true});
            skLineSegment(sketch, "E337", {"start": v(-15.24, -15.25) * mm, "end": v(0, 0) * mm, "construction": true});
            skCircle(sketch, "E338", {"center": v(15.26, 15.25) * mm, "radius": 5 * mm, "construction": true});
            skCircle(sketch, "E339", {"center": v(-15.24, 15.25) * mm, "radius": 5 * mm, "construction": true});
            skCircle(sketch, "E340", {"center": v(-15.24, -15.25) * mm, "radius": 5 * mm, "construction": true});
            skCircle(sketch, "E341", {"center": v(15.26, -15.25) * mm, "radius": 5 * mm, "construction": true});
            skLineSegment(sketch, "E342.bottom", {"start": v(-5.65, -5.65) * mm, "end": v(5.66, -5.65) * mm, "construction": true});
            skLineSegment(sketch, "E342.top", {"start": v(-5.65, 5.66) * mm, "end": v(5.66, 5.66) * mm, "construction": true});
            skLineSegment(sketch, "E342.left", {"start": v(-5.65, -5.65) * mm, "end": v(-5.65, 5.66) * mm, "construction": true});
            skLineSegment(sketch, "E342.right", {"start": v(5.66, -5.65) * mm, "end": v(5.66, 5.66) * mm, "construction": true});
            skPoint(sketch, "E343", {"position": v(0, 5.66) * mm});
            skPoint(sketch, "E344", {"position": v(5.66, 0) * mm});
            skPoint(sketch, "E345", {"position": v(-5.65, 0) * mm});
            skPoint(sketch, "E346", {"position": v(0, -5.65) * mm});
            skLineSegment(sketch, "E347", {"start": v(15.26, 15.25) * mm, "end": v(70.97, 70.96) * mm, "construction": true});
            skLineSegment(sketch, "E348", {"start": v(61.07, 61.06) * mm, "end": v(56.12, 66.01) * mm, "construction": true});
            skLineSegment(sketch, "E349", {"start": v(61.07, 61.06) * mm, "end": v(66.02, 56.11) * mm, "construction": true});
            skCircle(sketch, "E350", {"center": v(70.97, 70.96) * mm, "radius": 23.5 * mm, "construction": true});
            skLineSegment(sketch, "E351", {"start": v(70.97, 70.96) * mm, "end": v(70.97, 94.46) * mm, "construction": true});
            skLineSegment(sketch, "E352", {"start": v(70.97, 70.96) * mm, "end": v(94.47, 70.96) * mm, "construction": true});
            skLineSegment(sketch, "E353", {"start": v(53.84, 63.73) * mm, "end": v(27.21, 37.1) * mm});
            skLineSegment(sketch, "E354", {"start": v(63.66, 53.75) * mm, "end": v(37.11, 27.2) * mm});
            skCircle(sketch, "E355", {"center": v(70.97, 70.96) * mm, "radius": 15.5 * mm, "construction": true});
            skLineSegment(sketch, "E356", {"start": v(70.97, 70.96) * mm, "end": v(54.35, 87.58) * mm, "construction": true});
            skLineSegment(sketch, "E357", {"start": v(70.97, 70.96) * mm, "end": v(87.59, 54.34) * mm, "construction": true});
            skLineSegment(sketch, "E358", {"start": v(70.97, 70.96) * mm, "end": v(87.59, 87.58) * mm, "construction": true});
            skLineSegment(sketch, "E359", {"start": v(87.59, 54.34) * mm, "end": v(93, 62.76) * mm, "construction": true});
            skLineSegment(sketch, "E360", {"start": v(87.59, 87.58) * mm, "end": v(90.73, 83.69) * mm, "construction": true});
            skLineSegment(sketch, "E361", {"start": v(87.59, 87.58) * mm, "end": v(83.7, 90.72) * mm, "construction": true});
            skLineSegment(sketch, "E362", {"start": v(54.35, 87.58) * mm, "end": v(62.77, 92.98) * mm, "construction": true});
            skCircle(sketch, "E363", {"center": v(70.97, 70.96) * mm, "radius": 20 * mm, "construction": true});
            skLineSegment(sketch, "E364", {"start": v(62.77, 92.98) * mm, "end": v(64.71, 89.96) * mm, "construction": true});
            skLineSegment(sketch, "E365", {"start": v(83.7, 90.72) * mm, "end": v(81.48, 87.97) * mm, "construction": true});
            skLineSegment(sketch, "E366", {"start": v(90.73, 83.69) * mm, "end": v(87.98, 81.47) * mm, "construction": true});
            skPoint(sketch, "E367", {"position": v(56.83, 85.1) * mm});
            skPoint(sketch, "E368", {"position": v(58.56, 90.28) * mm});
            skLineSegment(sketch, "E369", {"start": v(64.71, 89.96) * mm, "end": v(81.48, 87.97) * mm, "construction": true});
            skLineSegment(sketch, "E370", {"start": v(73.1, 88.96) * mm, "end": v(72.79, 86.35) * mm, "construction": true});
            skLineSegment(sketch, "E371", {"start": v(72.79, 86.35) * mm, "end": v(72.61, 84.86) * mm, "construction": true});
            skPoint(sketch, "E372", {"position": v(90.29, 58.55) * mm});
            skLineSegment(sketch, "E373", {"start": v(93, 62.76) * mm, "end": v(89.96, 64.7) * mm, "construction": true});
            skPoint(sketch, "E374", {"position": v(85.11, 56.82) * mm});
            skPoint(sketch, "E375.visualSharp", {"position": v(56.97, 70.96) * mm});
            skPoint(sketch, "E376.visualSharp", {"position": v(72.61, 84.86) * mm});
            skPoint(sketch, "E377.visualSharp", {"position": v(84.97, 70.96) * mm});
            skPoint(sketch, "E378.visualSharp", {"position": v(70.97, 56.84) * mm});
            skPoint(sketch, "E379.visualSharp", {"position": v(56.12, 66.01) * mm});
            skPoint(sketch, "E380.visualSharp", {"position": v(66.02, 56.11) * mm});
            skLineSegment(sketch, "E381", {"start": v(76.63, 76.62) * mm, "end": v(79.8, 79.8) * mm, "construction": true});
            skLineSegment(sketch, "E382", {"start": v(70.97, 90.26) * mm, "end": v(65.72, 90.26) * mm, "construction": true});
            skLineSegment(sketch, "E383", {"start": v(70.97, 90.26) * mm, "end": v(76.22, 90.26) * mm, "construction": true});
            skFitSpline(sketch, "E384", {"points": [v(65.72, 90.26) * mm, v(70.97, 94.46) * mm, v(76.22, 90.26) * mm], "startDerivative": vector(9, 14.06) * mm, "endDerivative": vector(9, -14.06) * mm});
            skLineSegment(sketch, "E385", {"start": v(70.97, 92.6) * mm, "end": v(74.72, 92.6) * mm, "construction": true});
            skLineSegment(sketch, "E386", {"start": v(70.97, 92.6) * mm, "end": v(67.22, 92.6) * mm, "construction": true});
            skLineSegment(sketch, "E387", {"start": v(65.72, 90.26) * mm, "end": v(61.07, 80.86) * mm});
            skPoint(sketch, "E388", {"position": v(57.94, 76.1) * mm});
            skArc(sketch, "E389", {"start": v(61.07, 80.86) * mm, "mid": v(58.04, 76.32) * mm, "end": v(56.97, 70.96) * mm});
            skPoint(sketch, "E390", {"position": v(84.09, 75.85) * mm});
            skFitSpline(sketch, "E391", {"points": [v(84.09, 75.85) * mm, v(90.97, 70.96) * mm, v(68.49, 55.66) * mm], "startDerivative": vector(24.48, -10.1) * mm, "endDerivative": vector(-49.92, -7.72) * mm});
            skFitSpline(sketch, "E392", {"points": [v(53.84, 63.73) * mm, v(56.97, 70.96) * mm], "startDerivative": vector(4.73, 4.42) * mm, "endDerivative": vector(1.47, 12.68) * mm});
            skLineSegment(sketch, "E393", {"start": v(16.8, 16.8) * mm, "end": v(13.62, 19.97) * mm, "construction": true});
            skLineSegment(sketch, "E394", {"start": v(16.8, 16.8) * mm, "end": v(19.98, 13.6) * mm, "construction": true});
            skLineSegment(sketch, "E395", {"start": v(37.11, 27.2) * mm, "end": v(33.3, 23.4) * mm, "construction": true});
            skLineSegment(sketch, "E396", {"start": v(27.21, 37.1) * mm, "end": v(23.4, 33.3) * mm, "construction": true});
            skLineSegment(sketch, "E397", {"start": v(23.4, 33.3) * mm, "end": v(13.62, 19.97) * mm});
            skLineSegment(sketch, "E398", {"start": v(33.3, 23.4) * mm, "end": v(19.98, 13.6) * mm});
            skPoint(sketch, "E399", {"position": v(25.01, 35.61) * mm});
            skPoint(sketch, "E400", {"position": v(35.69, 25.07) * mm});
            skArc(sketch, "E401", {"start": v(33.3, 23.4) * mm, "mid": v(35.56, 24.95) * mm, "end": v(37.11, 27.2) * mm});
            skArc(sketch, "E402", {"start": v(27.21, 37.1) * mm, "mid": v(24.96, 35.55) * mm, "end": v(23.4, 33.3) * mm});
            skLineSegment(sketch, "E403.bottom", {"start": v(0, 5.66) * mm, "end": v(6.37, 5.66) * mm, "construction": true});
            skLineSegment(sketch, "E403.top", {"start": v(0, 12.02) * mm, "end": v(6.37, 12.02) * mm, "construction": true});
            skLineSegment(sketch, "E403.left", {"start": v(0, 5.66) * mm, "end": v(0, 12.02) * mm, "construction": true});
            skLineSegment(sketch, "E403.right", {"start": v(6.37, 5.66) * mm, "end": v(6.37, 12.02) * mm, "construction": true});
            skLineSegment(sketch, "E404", {"start": v(0, 5.66) * mm, "end": v(6.37, 12.02) * mm});
            skLineSegment(sketch, "E405", {"start": v(6.37, 12.02) * mm, "end": v(10.3, 15.95) * mm});
            skLineSegment(sketch, "E406.bottom", {"start": v(5.66, 0) * mm, "end": v(12.02, 0) * mm, "construction": true});
            skLineSegment(sketch, "E406.top", {"start": v(5.66, 6.36) * mm, "end": v(12.02, 6.36) * mm, "construction": true});
            skLineSegment(sketch, "E406.left", {"start": v(5.66, 0) * mm, "end": v(5.66, 6.36) * mm, "construction": true});
            skLineSegment(sketch, "E406.right", {"start": v(12.02, 0) * mm, "end": v(12.02, 6.36) * mm, "construction": true});
            skLineSegment(sketch, "E407", {"start": v(5.66, 0) * mm, "end": v(12.02, 6.36) * mm});
            skLineSegment(sketch, "E408", {"start": v(12.02, 6.36) * mm, "end": v(15.96, 10.3) * mm});
            skPoint(sketch, "E409", {"position": v(11.75, 18.81) * mm});
            skPoint(sketch, "E410", {"position": v(19.05, 11.99) * mm});
            skArc(sketch, "E411", {"start": v(15.96, 10.3) * mm, "mid": v(18.44, 11.4) * mm, "end": v(19.98, 13.6) * mm});
            skArc(sketch, "E412", {"start": v(13.62, 19.97) * mm, "mid": v(11.4, 18.43) * mm, "end": v(10.3, 15.95) * mm});
            skLineSegment(sketch, "E413", {"start": v(0, 5.66) * mm, "end": v(0, 0) * mm});
            skLineSegment(sketch, "E414", {"start": v(0, 0) * mm, "end": v(5.66, 0) * mm});
            skCircle(sketch, "E415", {"center": v(30.26, 30.25) * mm, "radius": 1.5 * mm});
            skCircle(sketch, "E416", {"center": v(15.26, 15.25) * mm, "radius": 1.5 * mm});
            skPoint(sketch, "E417", {"position": v(70.97, 90.96) * mm});
            skLineSegment(sketch, "E418", {"start": v(70.97, 86.46) * mm, "end": v(67.3, 86.02) * mm, "construction": true});
            skLineSegment(sketch, "E419", {"start": v(70.97, 86.46) * mm, "end": v(74.64, 86.02) * mm, "construction": true});
            skLineSegment(sketch, "E420", {"start": v(74.64, 86.02) * mm, "end": v(75.81, 84.1) * mm, "construction": true});
            skLineSegment(sketch, "E421", {"start": v(67.3, 86.02) * mm, "end": v(66.13, 84.1) * mm, "construction": true});
            skPoint(sketch, "E422", {"position": v(75.81, 84.1) * mm});
            skPoint(sketch, "E423", {"position": v(66.13, 84.1) * mm});
            skPoint(sketch, "E424", {"position": v(70.97, 89.22) * mm});
            skLineSegment(sketch, "E425", {"start": v(67.3, 86.02) * mm, "end": v(67.48, 84.52) * mm, "construction": true});
            skLineSegment(sketch, "E426", {"start": v(74.64, 86.02) * mm, "end": v(74.46, 84.52) * mm, "construction": true});
            skLineSegment(sketch, "E427", {"start": v(67.48, 84.52) * mm, "end": v(67.6, 83.52) * mm, "construction": true});
            skLineSegment(sketch, "E428", {"start": v(74.46, 84.52) * mm, "end": v(74.34, 83.52) * mm, "construction": true});
            skFitSpline(sketch, "E429", {"points": [v(67.48, 84.52) * mm, v(70.97, 89.22) * mm, v(74.46, 84.52) * mm], "startDerivative": vector(6.99, 14.1) * mm, "endDerivative": vector(6.99, -14.1) * mm});
            skLineSegment(sketch, "E430", {"start": v(67.6, 83.52) * mm, "end": v(74.34, 83.52) * mm, "construction": true});
            skPoint(sketch, "E431", {"position": v(70.97, 83.52) * mm});
            skFitSpline(sketch, "E432", {"points": [v(67.48, 84.52) * mm, v(70.97, 83.52) * mm, v(74.46, 84.52) * mm], "startDerivative": vector(0.72, -5.96) * mm, "endDerivative": vector(0.72, 5.96) * mm});
            skCircle(sketch, "E433", {"center": v(70.97, 78.96) * mm, "radius": 1.5 * mm, "construction": true});
            skCircle(sketch, "E434", {"center": v(70.97, 80.46) * mm, "radius": 1.5 * mm, "construction": true});
            skCircle(sketch, "E435", {"center": v(78.97, 70.96) * mm, "radius": 1.5 * mm, "construction": true});
            skCircle(sketch, "E436", {"center": v(80.47, 70.96) * mm, "radius": 1.5 * mm, "construction": true});
            skCircle(sketch, "E437", {"center": v(70.97, 62.96) * mm, "radius": 1.5 * mm, "construction": true});
            skCircle(sketch, "E438", {"center": v(70.97, 61.46) * mm, "radius": 1.5 * mm, "construction": true});
            skCircle(sketch, "E439", {"center": v(62.97, 70.96) * mm, "radius": 1.5 * mm, "construction": true});
            skCircle(sketch, "E440", {"center": v(61.47, 70.96) * mm, "radius": 1.5 * mm, "construction": true});
            skPoint(sketch, "E441", {"position": v(72.27, 79.71) * mm});
            skPoint(sketch, "E442", {"position": v(69.67, 79.71) * mm});
            skPoint(sketch, "E443", {"position": v(70.97, 81.96) * mm});
            skPoint(sketch, "E444", {"position": v(70.97, 77.46) * mm});
            skArc(sketch, "E445", {"start": v(69.67, 79.71) * mm, "mid": v(70.97, 77.46) * mm, "end": v(72.27, 79.71) * mm});
            skArc(sketch, "E446", {"start": v(72.27, 79.71) * mm, "mid": v(70.97, 81.96) * mm, "end": v(69.67, 79.71) * mm});
            skPoint(sketch, "E447", {"position": v(77.47, 70.96) * mm});
            skPoint(sketch, "E448", {"position": v(79.72, 72.26) * mm});
            skPoint(sketch, "E449", {"position": v(79.72, 69.66) * mm});
            skPoint(sketch, "E450", {"position": v(81.97, 70.96) * mm});
            skPoint(sketch, "E451", {"position": v(70.97, 59.96) * mm});
            skPoint(sketch, "E452", {"position": v(70.97, 64.46) * mm});
            skPoint(sketch, "E453", {"position": v(69.67, 62.21) * mm});
            skPoint(sketch, "E454", {"position": v(72.27, 62.21) * mm});
            skPoint(sketch, "E455", {"position": v(62.22, 72.26) * mm});
            skPoint(sketch, "E456", {"position": v(62.22, 69.66) * mm});
            skPoint(sketch, "E457", {"position": v(59.97, 70.96) * mm});
            skPoint(sketch, "E458", {"position": v(64.47, 70.96) * mm});
            skArc(sketch, "E459", {"start": v(62.22, 69.66) * mm, "mid": v(64.47, 70.96) * mm, "end": v(62.22, 72.26) * mm});
            skArc(sketch, "E460", {"start": v(62.22, 72.26) * mm, "mid": v(59.97, 70.96) * mm, "end": v(62.22, 69.66) * mm});
            skArc(sketch, "E461", {"start": v(79.72, 72.26) * mm, "mid": v(77.47, 70.96) * mm, "end": v(79.72, 69.66) * mm});
            skArc(sketch, "E462", {"start": v(79.72, 69.66) * mm, "mid": v(81.97, 70.96) * mm, "end": v(79.72, 72.26) * mm});
            skArc(sketch, "E463", {"start": v(69.67, 62.21) * mm, "mid": v(70.97, 59.96) * mm, "end": v(72.27, 62.21) * mm});
            skArc(sketch, "E464", {"start": v(72.27, 62.21) * mm, "mid": v(70.97, 64.46) * mm, "end": v(69.67, 62.21) * mm});
            skLineSegment(sketch, "E465", {"start": v(76.22, 90.26) * mm, "end": v(80.87, 80.86) * mm});
            skPoint(sketch, "E466", {"position": v(82.74, 78.54) * mm});
            skArc(sketch, "E467", {"start": v(84.09, 75.85) * mm, "mid": v(82.75, 78.53) * mm, "end": v(80.87, 80.86) * mm});
            skPoint(sketch, "E468", {"position": v(84.95, 71.78) * mm});
            skPoint(sketch, "E469", {"position": v(86.47, 70.96) * mm});
            skPoint(sketch, "E470", {"position": v(82.4, 64.55) * mm});
            skFitSpline(sketch, "E471", {"points": [v(84.95, 71.78) * mm, v(86.47, 70.96) * mm, v(82.4, 64.55) * mm], "startDerivative": vector(7.9, -0.91) * mm, "endDerivative": vector(-10.03, -8.08) * mm});
            skPoint(sketch, "E472", {"position": v(83.76, 70.96) * mm});
            skFitSpline(sketch, "E473", {"points": [v(82.4, 64.55) * mm, v(83.76, 70.96) * mm, v(84.95, 71.78) * mm], "startDerivative": vector(-7.12, -6.6) * mm, "endDerivative": vector(6.93, -0.38) * mm});
            skFitSpline(sketch, "E474", {"points": [v(63.66, 53.75) * mm, v(68.49, 55.66) * mm], "startDerivative": vector(5.12, 3.73) * mm, "endDerivative": vector(5.29, 1) * mm});
            skSolve(sketch);
        }
        {
            var Q0;
            Q0 = qSketchRegion(id + "F0", true);
            extrude(context, id + "F2", {"entities" : qUnion([Q0]), "depth" : 2 * mm});
        }
        {
            var Q0;
            Q0=qCreatedBy(makeId("Top.planeOp"),FACE);
            var sketch = newSketch(context, id + "F3", { "sketchPlane" : qUnion([Q0])});
            skLineSegment(sketch, "E475.bottom", {"start": v(-15.25, 15.25) * mm, "end": v(15.25, 15.25) * mm, "construction": true});
            skLineSegment(sketch, "E475.top", {"start": v(-15.25, -15.25) * mm, "end": v(15.25, -15.25) * mm, "construction": true});
            skLineSegment(sketch, "E475.left", {"start": v(-15.25, 15.25) * mm, "end": v(-15.25, -15.25) * mm, "construction": true});
            skLineSegment(sketch, "E475.right", {"start": v(15.25, 15.25) * mm, "end": v(15.25, -15.25) * mm, "construction": true});
            skPoint(sketch, "E475.middle", {"position": v(0, 0) * mm});
            skLineSegment(sketch, "E476.bottom", {"start": v(30.25, 30.25) * mm, "end": v(-30.25, 30.25) * mm, "construction": true});
            skLineSegment(sketch, "E476.top", {"start": v(30.25, -30.25) * mm, "end": v(-30.25, -30.25) * mm, "construction": true});
            skLineSegment(sketch, "E476.left", {"start": v(30.25, 30.25) * mm, "end": v(30.25, -30.25) * mm, "construction": true});
            skLineSegment(sketch, "E476.right", {"start": v(-30.25, 30.25) * mm, "end": v(-30.25, -30.25) * mm, "construction": true});
            skLineSegment(sketch, "E477.bottom", {"start": v(-70.96, 70.96) * mm, "end": v(70.96, 70.96) * mm, "construction": true});
            skLineSegment(sketch, "E477.top", {"start": v(-70.96, -70.96) * mm, "end": v(70.96, -70.96) * mm, "construction": true});
            skLineSegment(sketch, "E477.left", {"start": v(-70.96, 70.96) * mm, "end": v(-70.96, -70.96) * mm, "construction": true});
            skLineSegment(sketch, "E477.right", {"start": v(70.96, 70.96) * mm, "end": v(70.96, -70.96) * mm, "construction": true});
            skCircle(sketch, "E478", {"center": v(70.96, 70.96) * mm, "radius": 4.5 * mm, "construction": true});
            skCircle(sketch, "E479", {"center": v(-70.96, 70.96) * mm, "radius": 4.5 * mm, "construction": true});
            skCircle(sketch, "E480", {"center": v(70.96, -70.96) * mm, "radius": 4.5 * mm, "construction": true});
            skCircle(sketch, "E481", {"center": v(-70.96, -70.96) * mm, "radius": 4.5 * mm, "construction": true});
            skCircle(sketch, "E482", {"center": v(70.96, 70.96) * mm, "radius": 8 * mm, "construction": true});
            skCircle(sketch, "E483", {"center": v(70.96, -70.96) * mm, "radius": 8 * mm, "construction": true});
            skCircle(sketch, "E484", {"center": v(-70.96, -70.96) * mm, "radius": 8 * mm, "construction": true});
            skCircle(sketch, "E485", {"center": v(-70.96, 70.96) * mm, "radius": 8 * mm, "construction": true});
            skCircle(sketch, "E486", {"center": v(70.96, 70.96) * mm, "radius": 9.5 * mm, "construction": true});
            skCircle(sketch, "E487", {"center": v(70.96, -70.96) * mm, "radius": 9.5 * mm, "construction": true});
            skCircle(sketch, "E488", {"center": v(-70.96, -70.96) * mm, "radius": 9.5 * mm, "construction": true});
            skCircle(sketch, "E489", {"center": v(-70.96, 70.96) * mm, "radius": 9.5 * mm, "construction": true});
            skCircle(sketch, "E490", {"center": v(70.96, 70.96) * mm, "radius": 14 * mm, "construction": true});
            skCircle(sketch, "E491", {"center": v(-70.96, 70.96) * mm, "radius": 14 * mm, "construction": true});
            skCircle(sketch, "E492", {"center": v(70.96, -70.96) * mm, "radius": 14 * mm, "construction": true});
            skCircle(sketch, "E493", {"center": v(-70.96, -70.96) * mm, "radius": 14 * mm, "construction": true});
            skCircle(sketch, "E494", {"center": v(70.96, 70.96) * mm, "radius": 63.5 * mm, "construction": true});
            skCircle(sketch, "E495", {"center": v(70.96, -70.96) * mm, "radius": 63.5 * mm, "construction": true});
            skCircle(sketch, "E496", {"center": v(-70.96, -70.96) * mm, "radius": 63.5 * mm, "construction": true});
            skCircle(sketch, "E497", {"center": v(-70.96, 70.96) * mm, "radius": 63.5 * mm, "construction": true});
            skLineSegment(sketch, "E498", {"start": v(0, 30.25) * mm, "end": v(0, 36.4) * mm, "construction": true});
            skLineSegment(sketch, "E499", {"start": v(0, 36.4) * mm, "end": v(-14.3, 36.4) * mm, "construction": true});
            skLineSegment(sketch, "E500", {"start": v(0, 36.4) * mm, "end": v(14.29, 36.4) * mm, "construction": true});
            skLineSegment(sketch, "E501", {"start": v(0, -30.25) * mm, "end": v(0, -36.4) * mm, "construction": true});
            skLineSegment(sketch, "E502", {"start": v(0, -36.4) * mm, "end": v(-14.29, -36.4) * mm, "construction": true});
            skLineSegment(sketch, "E503", {"start": v(0, -36.4) * mm, "end": v(14.3, -36.4) * mm, "construction": true});
            skLineSegment(sketch, "E504.bottom", {"start": v(-26.2, 26.2) * mm, "end": v(26.2, 26.2) * mm, "construction": true});
            skLineSegment(sketch, "E504.top", {"start": v(-26.2, -26.19) * mm, "end": v(26.2, -26.19) * mm, "construction": true});
            skLineSegment(sketch, "E504.left", {"start": v(-26.2, 26.2) * mm, "end": v(-26.2, -26.19) * mm, "construction": true});
            skLineSegment(sketch, "E504.right", {"start": v(26.2, 26.2) * mm, "end": v(26.2, -26.2) * mm, "construction": true});
            skCircle(sketch, "E505", {"center": v(30.25, 30.25) * mm, "radius": 5 * mm, "construction": true});
            skCircle(sketch, "E506", {"center": v(-30.25, 30.25) * mm, "radius": 5 * mm, "construction": true});
            skCircle(sketch, "E507", {"center": v(30.25, -30.25) * mm, "radius": 5 * mm, "construction": true});
            skCircle(sketch, "E508", {"center": v(-30.25, -30.25) * mm, "radius": 5 * mm, "construction": true});
            skLineSegment(sketch, "E509", {"start": v(-26.19, 26.2) * mm, "end": v(-30.25, 30.25) * mm, "construction": true});
            skLineSegment(sketch, "E510", {"start": v(-26.71, 26.71) * mm, "end": v(-33.79, 33.79) * mm, "construction": true});
            skLineSegment(sketch, "E511", {"start": v(-31.46, 31.46) * mm, "end": v(-28.13, 34.78) * mm, "construction": true});
            skLineSegment(sketch, "E512", {"start": v(-31.46, 31.46) * mm, "end": v(-34.78, 28.13) * mm, "construction": true});
            skLineSegment(sketch, "E513", {"start": v(26.2, 26.2) * mm, "end": v(30.25, 30.25) * mm, "construction": true});
            skLineSegment(sketch, "E514", {"start": v(26.71, 26.71) * mm, "end": v(33.79, 33.79) * mm, "construction": true});
            skLineSegment(sketch, "E515", {"start": v(31.46, 31.46) * mm, "end": v(34.78, 28.13) * mm, "construction": true});
            skLineSegment(sketch, "E516", {"start": v(31.46, 31.46) * mm, "end": v(28.13, 34.78) * mm, "construction": true});
            skLineSegment(sketch, "E517", {"start": v(26.19, -26.19) * mm, "end": v(30.25, -30.25) * mm, "construction": true});
            skLineSegment(sketch, "E518", {"start": v(26.71, -26.71) * mm, "end": v(33.79, -33.79) * mm, "construction": true});
            skLineSegment(sketch, "E519", {"start": v(31.46, -31.46) * mm, "end": v(34.78, -28.13) * mm, "construction": true});
            skLineSegment(sketch, "E520", {"start": v(31.46, -31.46) * mm, "end": v(28.13, -34.78) * mm, "construction": true});
            skLineSegment(sketch, "E521", {"start": v(-26.2, -26.2) * mm, "end": v(-30.25, -30.25) * mm, "construction": true});
            skLineSegment(sketch, "E522", {"start": v(-26.71, -26.71) * mm, "end": v(-33.79, -33.79) * mm, "construction": true});
            skLineSegment(sketch, "E523", {"start": v(-31.46, -31.46) * mm, "end": v(-28.13, -34.78) * mm, "construction": true});
            skLineSegment(sketch, "E524", {"start": v(-31.46, -31.46) * mm, "end": v(-34.78, -28.13) * mm, "construction": true});
            skArc(sketch, "E525", {"start": v(-28.13, 34.78) * mm, "mid": v(-33.79, 33.79) * mm, "end": v(-34.78, 28.13) * mm});
            skArc(sketch, "E526", {"start": v(34.78, 28.13) * mm, "mid": v(33.79, 33.79) * mm, "end": v(28.13, 34.78) * mm});
            skArc(sketch, "E527", {"start": v(28.13, -34.78) * mm, "mid": v(33.79, -33.79) * mm, "end": v(34.78, -28.13) * mm});
            skArc(sketch, "E528", {"start": v(-34.78, -28.13) * mm, "mid": v(-33.79, -33.79) * mm, "end": v(-28.13, -34.78) * mm});
            skLineSegment(sketch, "E529.bottom", {"start": v(24.5, -24.5) * mm, "end": v(-24.5, -24.5) * mm, "construction": true});
            skLineSegment(sketch, "E529.top", {"start": v(24.5, 24.5) * mm, "end": v(-24.5, 24.5) * mm, "construction": true});
            skLineSegment(sketch, "E529.left", {"start": v(24.5, -24.5) * mm, "end": v(24.5, 24.5) * mm, "construction": true});
            skLineSegment(sketch, "E529.right", {"start": v(-24.5, -24.5) * mm, "end": v(-24.5, 24.5) * mm, "construction": true});
            skLineSegment(sketch, "E530", {"start": v(34.78, 28.13) * mm, "end": v(28.26, 10.3) * mm});
            skLineSegment(sketch, "E531", {"start": v(28.26, -10.3) * mm, "end": v(34.78, -28.13) * mm});
            skLineSegment(sketch, "E532", {"start": v(-34.78, -28.13) * mm, "end": v(-28.26, -10.3) * mm});
            skLineSegment(sketch, "E533", {"start": v(-28.26, 10.3) * mm, "end": v(-34.78, 28.13) * mm});
            skPoint(sketch, "E534.visualSharp", {"position": v(24.5, 0) * mm});
            skArc(sketch, "E534.filletArc", {"start": v(28.26, 10.3) * mm, "mid": v(26.44, 0) * mm, "end": v(28.26, -10.3) * mm});
            skPoint(sketch, "E535.visualSharp", {"position": v(-24.5, 0) * mm});
            skArc(sketch, "E535.filletArc", {"start": v(-28.26, -10.3) * mm, "mid": v(-26.44, 0) * mm, "end": v(-28.26, 10.3) * mm});
            skPoint(sketch, "E536.visualSharp", {"position": v(0, -24.5) * mm});
            skLineSegment(sketch, "E537", {"start": v(-28.13, 34.78) * mm, "end": v(-11.4, 23.17) * mm});
            skLineSegment(sketch, "E538", {"start": v(11.4, 23.17) * mm, "end": v(28.13, 34.78) * mm});
            skPoint(sketch, "E539.visualSharp", {"position": v(0, 15.25) * mm});
            skArc(sketch, "E539.filletArc", {"start": v(-11.4, 23.17) * mm, "mid": v(0, 19.6) * mm, "end": v(11.4, 23.17) * mm});
            skCircle(sketch, "E540", {"center": v(-30.25, 30.25) * mm, "radius": 1.5 * mm});
            skCircle(sketch, "E541", {"center": v(-15.25, 15.25) * mm, "radius": 1.5 * mm});
            skCircle(sketch, "E542", {"center": v(15.25, 15.25) * mm, "radius": 1.5 * mm});
            skCircle(sketch, "E543", {"center": v(30.25, 30.25) * mm, "radius": 1.5 * mm});
            skCircle(sketch, "E544", {"center": v(30.25, -30.25) * mm, "radius": 1.5 * mm});
            skCircle(sketch, "E545", {"center": v(15.25, -15.25) * mm, "radius": 1.5 * mm});
            skCircle(sketch, "E546", {"center": v(-15.25, -15.25) * mm, "radius": 1.5 * mm});
            skCircle(sketch, "E547", {"center": v(-30.25, -30.25) * mm, "radius": 1.5 * mm});
            skLineSegment(sketch, "E548", {"start": v(-28.13, -34.78) * mm, "end": v(-11.4, -23.17) * mm});
            skLineSegment(sketch, "E549", {"start": v(11.4, -23.17) * mm, "end": v(28.13, -34.78) * mm});
            skPoint(sketch, "E550.visualSharp", {"position": v(0, -15.25) * mm});
            skArc(sketch, "E550.filletArc", {"start": v(11.4, -23.17) * mm, "mid": v(0, -19.6) * mm, "end": v(-11.4, -23.17) * mm});
            skSolve(sketch);
        }
        {
            var Q0;
            Q0 = qSketchRegion(id + "F1", true);
            extrude(context, id + "F4", {"entities" : qUnion([Q0]), "operationType" : NewBodyOperationType.ADD, "depth" : 7 * mm, "hasSecondDirection" : true, "secondDirectionOppositeDirection" : false, "secondDirectionDepth" : 3 * mm});
        }
        {
            var Q0;
            Q0=qCreatedBy(makeId("Top.planeOp"),FACE);
            var sketch = newSketch(context, id + "F5", { "sketchPlane" : qUnion([Q0])});
            skLineSegment(sketch, "E551.bottom", {"start": v(-15.28, 17.52) * mm, "end": v(15.22, 17.52) * mm, "construction": true});
            skLineSegment(sketch, "E551.top", {"start": v(-15.25, -12.98) * mm, "end": v(15.25, -12.98) * mm, "construction": true});
            skLineSegment(sketch, "E551.left", {"start": v(-15.25, 17.52) * mm, "end": v(-15.25, -12.98) * mm, "construction": true});
            skLineSegment(sketch, "E551.right", {"start": v(15.22, 17.52) * mm, "end": v(15.22, -12.98) * mm, "construction": true});
            skPoint(sketch, "E551.middle", {"position": v(-0.01, 2.27) * mm});
            skLineSegment(sketch, "E552.bottom", {"start": v(30.24, 32.52) * mm, "end": v(-30.26, 32.52) * mm, "construction": true});
            skLineSegment(sketch, "E552.top", {"start": v(30.24, -27.98) * mm, "end": v(-30.26, -27.98) * mm, "construction": true});
            skLineSegment(sketch, "E552.left", {"start": v(30.24, 32.52) * mm, "end": v(30.24, -27.98) * mm, "construction": true});
            skLineSegment(sketch, "E552.right", {"start": v(-30.26, 32.52) * mm, "end": v(-30.26, -27.98) * mm, "construction": true});
            skLineSegment(sketch, "E553.bottom", {"start": v(-70.97, 73.23) * mm, "end": v(70.95, 73.23) * mm, "construction": true});
            skLineSegment(sketch, "E553.top", {"start": v(-70.97, -68.69) * mm, "end": v(70.95, -68.69) * mm, "construction": true});
            skLineSegment(sketch, "E553.left", {"start": v(-70.97, 73.23) * mm, "end": v(-70.97, -68.69) * mm, "construction": true});
            skLineSegment(sketch, "E553.right", {"start": v(70.95, 73.23) * mm, "end": v(70.95, -68.69) * mm, "construction": true});
            skCircle(sketch, "E554", {"center": v(70.95, 73.23) * mm, "radius": 8 * mm, "construction": true});
            skCircle(sketch, "E555", {"center": v(70.95, -68.69) * mm, "radius": 8 * mm, "construction": true});
            skCircle(sketch, "E556", {"center": v(-70.97, -68.69) * mm, "radius": 8 * mm, "construction": true});
            skCircle(sketch, "E557", {"center": v(-70.97, 73.23) * mm, "radius": 8 * mm, "construction": true});
            skCircle(sketch, "E558", {"center": v(70.95, 73.23) * mm, "radius": 9.5 * mm, "construction": true});
            skCircle(sketch, "E559", {"center": v(70.95, -68.69) * mm, "radius": 9.5 * mm, "construction": true});
            skCircle(sketch, "E560", {"center": v(-70.97, -68.69) * mm, "radius": 9.5 * mm, "construction": true});
            skCircle(sketch, "E561", {"center": v(-70.97, 73.23) * mm, "radius": 9.5 * mm, "construction": true});
            skCircle(sketch, "E562", {"center": v(70.95, 73.23) * mm, "radius": 14 * mm, "construction": true});
            skCircle(sketch, "E563", {"center": v(-70.97, 73.23) * mm, "radius": 14 * mm, "construction": true});
            skCircle(sketch, "E564", {"center": v(70.95, -68.69) * mm, "radius": 14 * mm, "construction": true});
            skCircle(sketch, "E565", {"center": v(-70.97, -68.69) * mm, "radius": 14 * mm, "construction": true});
            skCircle(sketch, "E566", {"center": v(70.95, 73.23) * mm, "radius": 63.5 * mm, "construction": true});
            skCircle(sketch, "E567", {"center": v(70.95, -68.69) * mm, "radius": 63.5 * mm, "construction": true});
            skCircle(sketch, "E568", {"center": v(-70.97, -68.69) * mm, "radius": 63.5 * mm, "construction": true});
            skCircle(sketch, "E569", {"center": v(-70.97, 73.23) * mm, "radius": 63.5 * mm, "construction": true});
            skLineSegment(sketch, "E570", {"start": v(-0.01, 32.52) * mm, "end": v(-0.01, 40.03) * mm, "construction": true});
            skLineSegment(sketch, "E571", {"start": v(-0.01, -27.98) * mm, "end": v(-0.01, -35.48) * mm, "construction": true});
            skLineSegment(sketch, "E572.bottom", {"start": v(-26.18, 28.53) * mm, "end": v(26.2, 28.53) * mm, "construction": true});
            skLineSegment(sketch, "E572.top", {"start": v(-26.22, -23.98) * mm, "end": v(26.16, -23.98) * mm, "construction": true});
            skLineSegment(sketch, "E572.left", {"start": v(-26.18, 28.53) * mm, "end": v(-26.18, -23.85) * mm, "construction": true});
            skLineSegment(sketch, "E572.right", {"start": v(26.2, 28.53) * mm, "end": v(26.2, -23.92) * mm, "construction": true});
            skCircle(sketch, "E573", {"center": v(30.24, 32.52) * mm, "radius": 5 * mm, "construction": true});
            skCircle(sketch, "E574", {"center": v(-30.26, 32.52) * mm, "radius": 5 * mm, "construction": true});
            skCircle(sketch, "E575", {"center": v(30.24, -27.98) * mm, "radius": 5 * mm, "construction": true});
            skCircle(sketch, "E576", {"center": v(-30.26, -27.98) * mm, "radius": 5 * mm, "construction": true});
            skLineSegment(sketch, "E577.bottom", {"start": v(24.49, 26.77) * mm, "end": v(-24.51, 26.77) * mm, "construction": true});
            skLineSegment(sketch, "E577.top", {"start": v(24.49, -22.23) * mm, "end": v(-24.51, -22.23) * mm, "construction": true});
            skLineSegment(sketch, "E577.left", {"start": v(24.49, 26.77) * mm, "end": v(24.49, -22.23) * mm, "construction": true});
            skLineSegment(sketch, "E577.right", {"start": v(-24.51, 26.77) * mm, "end": v(-24.51, -22.23) * mm, "construction": true});
            skLineSegment(sketch, "E578", {"start": v(-26.18, 28.53) * mm, "end": v(-30.26, 32.52) * mm, "construction": true});
            skLineSegment(sketch, "E579", {"start": v(-26.7, 29.02) * mm, "end": v(-33.83, 36.02) * mm, "construction": true});
            skLineSegment(sketch, "E580", {"start": v(-31.82, 34.05) * mm, "end": v(-28.67, 37.26) * mm, "construction": true});
            skLineSegment(sketch, "E581", {"start": v(-31.82, 34.05) * mm, "end": v(-34.97, 30.83) * mm, "construction": true});
            skArc(sketch, "E582", {"start": v(-28.67, 37.26) * mm, "mid": v(-33.83, 36.02) * mm, "end": v(-34.97, 30.83) * mm});
            skLineSegment(sketch, "E583", {"start": v(26.2, 28.53) * mm, "end": v(30.24, 32.52) * mm, "construction": true});
            skLineSegment(sketch, "E584", {"start": v(26.68, 29) * mm, "end": v(33.8, 36.04) * mm, "construction": true});
            skLineSegment(sketch, "E585", {"start": v(31.79, 34.06) * mm, "end": v(34.95, 30.86) * mm, "construction": true});
            skLineSegment(sketch, "E586", {"start": v(31.79, 34.06) * mm, "end": v(28.62, 37.26) * mm, "construction": true});
            skArc(sketch, "E587", {"start": v(34.95, 30.86) * mm, "mid": v(33.8, 36.04) * mm, "end": v(28.62, 37.26) * mm});
            skLineSegment(sketch, "E588", {"start": v(26.16, -23.98) * mm, "end": v(30.24, -27.98) * mm, "construction": true});
            skLineSegment(sketch, "E589", {"start": v(26.67, -24.48) * mm, "end": v(33.8, -31.48) * mm, "construction": true});
            skLineSegment(sketch, "E590", {"start": v(31.8, -29.5) * mm, "end": v(34.94, -26.29) * mm, "construction": true});
            skLineSegment(sketch, "E591", {"start": v(31.8, -29.5) * mm, "end": v(28.64, -32.72) * mm, "construction": true});
            skArc(sketch, "E592", {"start": v(28.64, -32.72) * mm, "mid": v(33.8, -31.48) * mm, "end": v(34.94, -26.29) * mm});
            skLineSegment(sketch, "E593", {"start": v(-26.22, -23.98) * mm, "end": v(-30.26, -27.98) * mm, "construction": true});
            skLineSegment(sketch, "E594", {"start": v(-26.7, -24.46) * mm, "end": v(-33.82, -31.5) * mm, "construction": true});
            skLineSegment(sketch, "E595", {"start": v(-31.81, -29.5) * mm, "end": v(-28.65, -32.7) * mm, "construction": true});
            skLineSegment(sketch, "E596", {"start": v(-31.81, -29.5) * mm, "end": v(-34.98, -26.31) * mm, "construction": true});
            skArc(sketch, "E597", {"start": v(-34.98, -26.31) * mm, "mid": v(-33.82, -31.5) * mm, "end": v(-28.65, -32.7) * mm});
            skLineSegment(sketch, "E598", {"start": v(-34.98, -26.31) * mm, "end": v(-28.29, -8.04) * mm});
            skLineSegment(sketch, "E599", {"start": v(-28.29, 12.59) * mm, "end": v(-34.97, 30.83) * mm});
            skLineSegment(sketch, "E600", {"start": v(34.95, 30.86) * mm, "end": v(28.26, 12.59) * mm});
            skLineSegment(sketch, "E601", {"start": v(28.26, -8.04) * mm, "end": v(34.94, -26.29) * mm});
            skPoint(sketch, "E602.visualSharp", {"position": v(24.49, 2.27) * mm});
            skArc(sketch, "E602.filletArc", {"start": v(28.26, 12.59) * mm, "mid": v(26.43, 2.27) * mm, "end": v(28.26, -8.04) * mm});
            skPoint(sketch, "E603.visualSharp", {"position": v(-24.51, 2.27) * mm});
            skArc(sketch, "E603.filletArc", {"start": v(-28.29, -8.04) * mm, "mid": v(-26.46, 2.27) * mm, "end": v(-28.29, 12.59) * mm});
            skLineSegment(sketch, "E604", {"start": v(-15.28, 22) * mm, "end": v(15.22, 22) * mm, "construction": true});
            skPoint(sketch, "E605.endSnap0", {"position": v(0, -12.98) * mm});
            skLineSegment(sketch, "E606", {"start": v(-15.25, -17.43) * mm, "end": v(15.25, -17.43) * mm, "construction": true});
            skLineSegment(sketch, "E607", {"start": v(-14.34, -35.48) * mm, "end": v(14.32, -35.48) * mm, "construction": true});
            skCircle(sketch, "E608", {"center": v(-30.26, 32.52) * mm, "radius": 1.5 * mm});
            skCircle(sketch, "E609", {"center": v(30.24, 32.52) * mm, "radius": 1.5 * mm});
            skCircle(sketch, "E610", {"center": v(15.22, 17.52) * mm, "radius": 1.5 * mm});
            skCircle(sketch, "E611", {"center": v(-15.28, 17.52) * mm, "radius": 1.5 * mm});
            skCircle(sketch, "E612", {"center": v(-15.25, -12.98) * mm, "radius": 1.5 * mm});
            skCircle(sketch, "E613", {"center": v(15.25, -12.98) * mm, "radius": 1.5 * mm});
            skCircle(sketch, "E614", {"center": v(30.24, -27.98) * mm, "radius": 1.5 * mm});
            skCircle(sketch, "E615", {"center": v(-30.26, -27.98) * mm, "radius": 1.5 * mm});
            skLineSegment(sketch, "E616", {"start": v(14.32, 40.03) * mm, "end": v(10.32, 40.03) * mm, "construction": true});
            skLineSegment(sketch, "E617", {"start": v(-14.34, 40.03) * mm, "end": v(-10.34, 40.03) * mm, "construction": true});
            skLineSegment(sketch, "E618", {"start": v(10.32, 40.03) * mm, "end": v(10.32, 36.03) * mm, "construction": true});
            skLineSegment(sketch, "E619", {"start": v(-10.34, 40.03) * mm, "end": v(-10.34, 36.03) * mm, "construction": true});
            skLineSegment(sketch, "E620", {"start": v(-0.01, 40.03) * mm, "end": v(-0.03, 17.52) * mm, "construction": true});
            skPoint(sketch, "E621.visualSharp", {"position": v(-14.34, -35.48) * mm});
            skPoint(sketch, "E622.visualSharp", {"position": v(14.32, -35.48) * mm});
            skCircle(sketch, "E623", {"center": v(-0.01, 2.27) * mm, "radius": 17.1 * mm, "construction": true});
            skLineSegment(sketch, "E624", {"start": v(-0.01, 2.27) * mm, "end": v(14.08, 16.37) * mm, "construction": true});
            skLineSegment(sketch, "E625", {"start": v(-0.01, 2.27) * mm, "end": v(-15.28, 17.52) * mm, "construction": true});
            skLineSegment(sketch, "E626", {"start": v(-0.01, 2.27) * mm, "end": v(-15.32, -13.05) * mm, "construction": true});
            skLineSegment(sketch, "E627", {"start": v(-0.01, 2.27) * mm, "end": v(15.25, -12.98) * mm, "construction": true});
            skLineSegment(sketch, "E628", {"start": v(-10.71, 12.96) * mm, "end": v(-7.89, 15.8) * mm, "construction": true});
            skLineSegment(sketch, "E629", {"start": v(-10.71, 12.96) * mm, "end": v(-13.54, 10.13) * mm, "construction": true});
            skLineSegment(sketch, "E630", {"start": v(9.01, 11.3) * mm, "end": v(11.84, 8.47) * mm, "construction": true});
            skLineSegment(sketch, "E631", {"start": v(9.01, 11.3) * mm, "end": v(6.19, 14.13) * mm, "construction": true});
            skLineSegment(sketch, "E632", {"start": v(9.8, -7.53) * mm, "end": v(12.63, -4.7) * mm, "construction": true});
            skLineSegment(sketch, "E633", {"start": v(9.8, -7.53) * mm, "end": v(6.97, -10.36) * mm, "construction": true});
            skLineSegment(sketch, "E634", {"start": v(-9.52, -7.25) * mm, "end": v(-6.7, -10.07) * mm, "construction": true});
            skLineSegment(sketch, "E635", {"start": v(-9.52, -7.25) * mm, "end": v(-12.35, -4.42) * mm, "construction": true});
            skLineSegment(sketch, "E636.bottom", {"start": v(6.34, 8.62) * mm, "end": v(-6.36, 8.62) * mm, "construction": true});
            skLineSegment(sketch, "E636.top", {"start": v(6.34, -4.08) * mm, "end": v(-6.36, -4.08) * mm, "construction": true});
            skLineSegment(sketch, "E636.left", {"start": v(6.34, 8.62) * mm, "end": v(6.34, -4.08) * mm, "construction": true});
            skLineSegment(sketch, "E636.right", {"start": v(-6.36, 8.62) * mm, "end": v(-6.36, -4.08) * mm, "construction": true});
            skLineSegment(sketch, "E637", {"start": v(6.19, 14.13) * mm, "end": v(8.92, 16.86) * mm, "construction": true});
            skLineSegment(sketch, "E638", {"start": v(11.84, 8.47) * mm, "end": v(14.57, 11.2) * mm, "construction": true});
            skLineSegment(sketch, "E639", {"start": v(7.98, 15.92) * mm, "end": v(1.4, 9.34) * mm});
            skLineSegment(sketch, "E640", {"start": v(-1.43, 9.34) * mm, "end": v(-8, 15.92) * mm});
            skLineSegment(sketch, "E641", {"start": v(-13.54, 10.13) * mm, "end": v(-14.6, 11.2) * mm, "construction": true});
            skLineSegment(sketch, "E642", {"start": v(-6.7, -10.07) * mm, "end": v(-8.93, -12.32) * mm, "construction": true});
            skLineSegment(sketch, "E643", {"start": v(-8, -11.38) * mm, "end": v(-1.43, -4.8) * mm});
            skLineSegment(sketch, "E644", {"start": v(1.4, -4.8) * mm, "end": v(7.98, -11.37) * mm});
            skLineSegment(sketch, "E645", {"start": v(13.64, 10.27) * mm, "end": v(7.06, 3.69) * mm});
            skLineSegment(sketch, "E646", {"start": v(7.06, 0.86) * mm, "end": v(13.64, -5.72) * mm});
            skPoint(sketch, "E647", {"position": v(-7.75, 17.52) * mm});
            skPoint(sketch, "E648", {"position": v(7.72, 17.52) * mm});
            skPoint(sketch, "E649", {"position": v(15.22, 10.04) * mm});
            skPoint(sketch, "E650", {"position": v(15.22, -5.5) * mm});
            skPoint(sketch, "E651", {"position": v(7.72, -12.98) * mm});
            skPoint(sketch, "E652", {"position": v(-7.75, -12.98) * mm});
            skPoint(sketch, "E653", {"position": v(-15.25, -5.5) * mm});
            skPoint(sketch, "E654", {"position": v(-15.25, 10.04) * mm});
            skLineSegment(sketch, "E655", {"start": v(-7.79, 17.5) * mm, "end": v(-7.75, 17.52) * mm});
            skLineSegment(sketch, "E656", {"start": v(7.76, 17.5) * mm, "end": v(7.72, 17.52) * mm});
            skLineSegment(sketch, "E657", {"start": v(15.22, 10.05) * mm, "end": v(15.22, 10.04) * mm});
            skLineSegment(sketch, "E658", {"start": v(15.22, -5.5) * mm, "end": v(15.22, -5.5) * mm});
            skLineSegment(sketch, "E659", {"start": v(7.76, -12.96) * mm, "end": v(7.72, -12.98) * mm});
            skLineSegment(sketch, "E660", {"start": v(-7.75, -12.98) * mm, "end": v(-7.78, -12.96) * mm});
            skLineSegment(sketch, "E661", {"start": v(-15.24, -5.5) * mm, "end": v(-15.25, -5.5) * mm});
            skLineSegment(sketch, "E662", {"start": v(-15.24, 10.05) * mm, "end": v(-15.25, 10.04) * mm});
            skPoint(sketch, "E663", {"position": v(-0.03, 19.37) * mm});
            skPoint(sketch, "E664", {"position": v(17.09, 2.27) * mm});
            skPoint(sketch, "E665", {"position": v(-17.11, 2.27) * mm});
            skPoint(sketch, "E666", {"position": v(-0.01, -14.83) * mm});
            skArc(sketch, "E667", {"start": v(15.22, -5.5) * mm, "mid": v(17.09, 2.27) * mm, "end": v(15.22, 10.04) * mm});
            skArc(sketch, "E668", {"start": v(-15.25, 10.04) * mm, "mid": v(-17.11, 2.27) * mm, "end": v(-15.25, -5.5) * mm});
            skPoint(sketch, "E669.visualSharp", {"position": v(-5.66, 2.27) * mm});
            skPoint(sketch, "E670.visualSharp", {"position": v(-14.6, 11.2) * mm});
            skArc(sketch, "E670.filletArc", {"start": v(-13.66, 10.27) * mm, "mid": v(-14.5, 10.55) * mm, "end": v(-15.24, 10.05) * mm});
            skPoint(sketch, "E671.visualSharp", {"position": v(-14.6, -6.66) * mm});
            skArc(sketch, "E671.filletArc", {"start": v(-15.24, -5.5) * mm, "mid": v(-14.5, -6.01) * mm, "end": v(-13.66, -5.73) * mm});
            skPoint(sketch, "E672.visualSharp", {"position": v(-8.94, 16.86) * mm});
            skArc(sketch, "E672.filletArc", {"start": v(-7.79, 17.5) * mm, "mid": v(-8.3, 16.77) * mm, "end": v(-8, 15.92) * mm});
            skPoint(sketch, "E673.visualSharp", {"position": v(8.92, 16.86) * mm});
            skArc(sketch, "E673.filletArc", {"start": v(7.98, 15.92) * mm, "mid": v(8.26, 16.77) * mm, "end": v(7.76, 17.5) * mm});
            skPoint(sketch, "E674.visualSharp", {"position": v(14.57, -6.66) * mm});
            skArc(sketch, "E674.filletArc", {"start": v(13.64, -5.72) * mm, "mid": v(14.48, -6) * mm, "end": v(15.22, -5.5) * mm});
            skPoint(sketch, "E675.visualSharp", {"position": v(14.57, 11.2) * mm});
            skArc(sketch, "E675.filletArc", {"start": v(15.22, 10.05) * mm, "mid": v(14.48, 10.55) * mm, "end": v(13.64, 10.27) * mm});
            skPoint(sketch, "E676.visualSharp", {"position": v(8.92, -12.3) * mm});
            skArc(sketch, "E676.filletArc", {"start": v(7.76, -12.96) * mm, "mid": v(8.27, -12.22) * mm, "end": v(7.98, -11.37) * mm});
            skPoint(sketch, "E677.visualSharp", {"position": v(-8.93, -12.32) * mm});
            skArc(sketch, "E677.filletArc", {"start": v(-8, -11.38) * mm, "mid": v(-8.28, -12.23) * mm, "end": v(-7.78, -12.96) * mm});
            skLineSegment(sketch, "E678", {"start": v(-13.66, 10.27) * mm, "end": v(-7.08, 3.68) * mm});
            skLineSegment(sketch, "E679", {"start": v(-13.66, -5.73) * mm, "end": v(-7.08, 0.86) * mm});
            skArc(sketch, "E680.filletArc", {"start": v(-7.08, 0.86) * mm, "mid": v(-6.5, 2.27) * mm, "end": v(-7.08, 3.68) * mm});
            skPoint(sketch, "E681.visualSharp", {"position": v(-0.01, -3.39) * mm});
            skArc(sketch, "E681.filletArc", {"start": v(1.4, -4.8) * mm, "mid": v(-0.01, -4.22) * mm, "end": v(-1.43, -4.8) * mm});
            skPoint(sketch, "E682.visualSharp", {"position": v(5.64, 2.27) * mm});
            skArc(sketch, "E682.filletArc", {"start": v(7.06, 3.69) * mm, "mid": v(6.47, 2.27) * mm, "end": v(7.06, 0.86) * mm});
            skPoint(sketch, "E683.visualSharp", {"position": v(-0.02, 7.93) * mm});
            skArc(sketch, "E683.filletArc", {"start": v(-1.43, 9.34) * mm, "mid": v(-0.02, 8.76) * mm, "end": v(1.4, 9.34) * mm});
            skLineSegment(sketch, "E684", {"start": v(-12.93, 15.17) * mm, "end": v(-11.16, 16.94) * mm, "construction": true});
            skLineSegment(sketch, "E685", {"start": v(-12.93, 15.17) * mm, "end": v(-14.7, 13.4) * mm, "construction": true});
            skLineSegment(sketch, "E686", {"start": v(-14.7, 13.4) * mm, "end": v(-27.43, 26.13) * mm, "construction": true});
            skPoint(sketch, "E687", {"position": v(-17.59, 16.3) * mm});
            skCircle(sketch, "E688", {"center": v(-15.28, 17.52) * mm, "radius": 4.62 * mm, "construction": true});
            skLineSegment(sketch, "E689", {"start": v(-27.43, 26.13) * mm, "end": v(-21.13, 10.9) * mm, "construction": true});
            skLineSegment(sketch, "E690", {"start": v(-15.28, 17.52) * mm, "end": v(-21.35, 11.45) * mm, "construction": true});
            skLineSegment(sketch, "E691", {"start": v(-18.88, 13.92) * mm, "end": v(-19.76, 13.03) * mm});
            skLineSegment(sketch, "E692", {"start": v(-22.2, 13.52) * mm, "end": v(-25.5, 21.5) * mm});
            skLineSegment(sketch, "E693", {"start": v(-23.88, 22.58) * mm, "end": v(-20.07, 18.78) * mm});
            skLineSegment(sketch, "E694", {"start": v(-19.86, 18.13) * mm, "end": v(-19.88, 18.01) * mm});
            skLineSegment(sketch, "E695", {"start": v(-18.86, 14.6) * mm, "end": v(-18.88, 14.62) * mm});
            skPoint(sketch, "E696", {"position": v(-19.7, 16.17) * mm});
            skArc(sketch, "E697", {"start": v(-19.88, 18.01) * mm, "mid": v(-19.72, 16.22) * mm, "end": v(-18.88, 14.62) * mm});
            skPoint(sketch, "E698.visualSharp", {"position": v(-27.43, 26.13) * mm});
            skArc(sketch, "E698.filletArc", {"start": v(-23.88, 22.58) * mm, "mid": v(-25.14, 22.7) * mm, "end": v(-25.5, 21.5) * mm});
            skPoint(sketch, "E699.visualSharp", {"position": v(-21.35, 11.45) * mm});
            skArc(sketch, "E699.filletArc", {"start": v(-22.2, 13.52) * mm, "mid": v(-21.12, 12.62) * mm, "end": v(-19.76, 13.03) * mm});
            skPoint(sketch, "E700.visualSharp", {"position": v(-18.55, 14.25) * mm});
            skArc(sketch, "E700.filletArc", {"start": v(-18.88, 13.92) * mm, "mid": v(-18.74, 14.26) * mm, "end": v(-18.86, 14.6) * mm});
            skPoint(sketch, "E701.visualSharp", {"position": v(-19.8, 18.5) * mm});
            skArc(sketch, "E701.filletArc", {"start": v(-19.86, 18.13) * mm, "mid": v(-19.89, 18.48) * mm, "end": v(-20.07, 18.78) * mm});
            skCircle(sketch, "E702", {"center": v(15.22, 17.54) * mm, "radius": 4.62 * mm, "construction": true});
            skLineSegment(sketch, "E703", {"start": v(15.22, 17.54) * mm, "end": v(12.89, 15.18) * mm, "construction": true});
            skLineSegment(sketch, "E704", {"start": v(12.89, 15.18) * mm, "end": v(14.67, 13.42) * mm, "construction": true});
            skLineSegment(sketch, "E705", {"start": v(12.89, 15.18) * mm, "end": v(11.1, 16.93) * mm, "construction": true});
            skLineSegment(sketch, "E706", {"start": v(11.1, 16.93) * mm, "end": v(23.84, 29.66) * mm, "construction": true});
            skLineSegment(sketch, "E707", {"start": v(14.67, 13.42) * mm, "end": v(27.3, 26.24) * mm, "construction": true});
            skLineSegment(sketch, "E708", {"start": v(15.22, 17.52) * mm, "end": v(21.34, 11.5) * mm, "construction": true});
            skLineSegment(sketch, "E709", {"start": v(21.34, 11.5) * mm, "end": v(27.3, 26.24) * mm, "construction": true});
            skLineSegment(sketch, "E710", {"start": v(19.8, 18.17) * mm, "end": v(19.81, 18.06) * mm});
            skLineSegment(sketch, "E711", {"start": v(18.82, 14.64) * mm, "end": v(18.84, 14.66) * mm});
            skLineSegment(sketch, "E712", {"start": v(20, 18.83) * mm, "end": v(23.79, 22.67) * mm});
            skLineSegment(sketch, "E713", {"start": v(25.43, 21.6) * mm, "end": v(22.18, 13.58) * mm});
            skLineSegment(sketch, "E714", {"start": v(19.74, 13.07) * mm, "end": v(18.84, 13.95) * mm});
            skPoint(sketch, "E715", {"position": v(19.64, 16.2) * mm});
            skArc(sketch, "E716", {"start": v(18.84, 14.66) * mm, "mid": v(19.66, 16.26) * mm, "end": v(19.81, 18.06) * mm});
            skPoint(sketch, "E717.visualSharp", {"position": v(18.5, 14.29) * mm});
            skArc(sketch, "E717.filletArc", {"start": v(18.82, 14.64) * mm, "mid": v(18.7, 14.3) * mm, "end": v(18.84, 13.95) * mm});
            skPoint(sketch, "E718.visualSharp", {"position": v(19.73, 18.55) * mm});
            skArc(sketch, "E718.filletArc", {"start": v(20, 18.83) * mm, "mid": v(19.82, 18.52) * mm, "end": v(19.8, 18.17) * mm});
            skPoint(sketch, "E719.visualSharp", {"position": v(27.3, 26.24) * mm});
            skArc(sketch, "E719.filletArc", {"start": v(25.43, 21.6) * mm, "mid": v(25.05, 22.8) * mm, "end": v(23.79, 22.67) * mm});
            skPoint(sketch, "E720.visualSharp", {"position": v(21.34, 11.5) * mm});
            skArc(sketch, "E720.filletArc", {"start": v(19.74, 13.07) * mm, "mid": v(21.1, 12.67) * mm, "end": v(22.18, 13.58) * mm});
            skCircle(sketch, "E721", {"center": v(-15.25, -12.98) * mm, "radius": 4.62 * mm, "construction": true});
            skCircle(sketch, "E722", {"center": v(15.25, -12.98) * mm, "radius": 4.62 * mm, "construction": true});
            skLineSegment(sketch, "E723", {"start": v(-15.25, -12.98) * mm, "end": v(-12.9, -10.63) * mm, "construction": true});
            skLineSegment(sketch, "E724", {"start": v(-12.9, -10.63) * mm, "end": v(-11.14, -12.4) * mm, "construction": true});
            skLineSegment(sketch, "E725", {"start": v(-12.9, -10.63) * mm, "end": v(-14.67, -8.87) * mm, "construction": true});
            skLineSegment(sketch, "E726", {"start": v(-11.14, -12.4) * mm, "end": v(-23.86, -25.13) * mm, "construction": true});
            skLineSegment(sketch, "E727", {"start": v(-14.67, -8.87) * mm, "end": v(-27.4, -21.6) * mm, "construction": true});
            skLineSegment(sketch, "E728", {"start": v(-15.25, -12.98) * mm, "end": v(-9.17, -19.05) * mm, "construction": true});
            skLineSegment(sketch, "E729", {"start": v(-15.25, -12.98) * mm, "end": v(-21.32, -6.9) * mm, "construction": true});
            skLineSegment(sketch, "E730", {"start": v(-25.48, -16.95) * mm, "end": v(-22.18, -8.98) * mm});
            skLineSegment(sketch, "E731", {"start": v(-19.73, -8.5) * mm, "end": v(-18.85, -9.37) * mm});
            skLineSegment(sketch, "E732", {"start": v(-23.85, -18.04) * mm, "end": v(-20.04, -14.23) * mm});
            skLineSegment(sketch, "E733", {"start": v(-18.83, -10.06) * mm, "end": v(-18.85, -10.08) * mm});
            skLineSegment(sketch, "E734", {"start": v(-19.83, -13.58) * mm, "end": v(-19.85, -13.47) * mm});
            skPoint(sketch, "E735", {"position": v(-19.68, -11.67) * mm});
            skArc(sketch, "E736", {"start": v(-18.85, -10.08) * mm, "mid": v(-19.68, -11.67) * mm, "end": v(-19.85, -13.47) * mm});
            skPoint(sketch, "E737.visualSharp", {"position": v(-18.52, -9.7) * mm});
            skArc(sketch, "E737.filletArc", {"start": v(-18.83, -10.06) * mm, "mid": v(-18.7, -9.71) * mm, "end": v(-18.85, -9.37) * mm});
            skPoint(sketch, "E738.visualSharp", {"position": v(-19.77, -13.96) * mm});
            skArc(sketch, "E738.filletArc", {"start": v(-20.04, -14.23) * mm, "mid": v(-19.85, -13.93) * mm, "end": v(-19.83, -13.58) * mm});
            skPoint(sketch, "E739.visualSharp", {"position": v(-27.4, -21.6) * mm});
            skArc(sketch, "E739.filletArc", {"start": v(-25.48, -16.95) * mm, "mid": v(-25.11, -18.17) * mm, "end": v(-23.85, -18.04) * mm});
            skPoint(sketch, "E740.visualSharp", {"position": v(-21.32, -6.9) * mm});
            skArc(sketch, "E740.filletArc", {"start": v(-19.73, -8.5) * mm, "mid": v(-21.09, -8.08) * mm, "end": v(-22.18, -8.98) * mm});
            skLineSegment(sketch, "E741", {"start": v(15.25, -12.98) * mm, "end": v(12.9, -10.63) * mm, "construction": true});
            skLineSegment(sketch, "E742", {"start": v(12.9, -10.63) * mm, "end": v(14.68, -8.87) * mm, "construction": true});
            skLineSegment(sketch, "E743", {"start": v(12.9, -10.63) * mm, "end": v(11.14, -12.4) * mm, "construction": true});
            skLineSegment(sketch, "E744", {"start": v(14.68, -8.87) * mm, "end": v(27.4, -21.59) * mm, "construction": true});
            skLineSegment(sketch, "E745", {"start": v(15.25, -12.98) * mm, "end": v(21.32, -6.9) * mm, "construction": true});
            skLineSegment(sketch, "E746", {"start": v(22.18, -8.97) * mm, "end": v(25.49, -16.95) * mm});
            skLineSegment(sketch, "E747", {"start": v(23.86, -18.04) * mm, "end": v(20.04, -14.23) * mm});
            skLineSegment(sketch, "E748", {"start": v(19.74, -8.49) * mm, "end": v(18.86, -9.37) * mm});
            skLineSegment(sketch, "E749", {"start": v(18.84, -10.06) * mm, "end": v(18.86, -10.08) * mm});
            skLineSegment(sketch, "E750", {"start": v(19.83, -13.58) * mm, "end": v(19.85, -13.46) * mm});
            skPoint(sketch, "E751", {"position": v(19.64, -11.53) * mm});
            skArc(sketch, "E752", {"start": v(19.85, -13.46) * mm, "mid": v(19.69, -11.67) * mm, "end": v(18.86, -10.08) * mm});
            skPoint(sketch, "E753.visualSharp", {"position": v(21.32, -6.9) * mm});
            skArc(sketch, "E753.filletArc", {"start": v(22.18, -8.97) * mm, "mid": v(21.1, -8.08) * mm, "end": v(19.74, -8.49) * mm});
            skPoint(sketch, "E754.visualSharp", {"position": v(19.77, -13.96) * mm});
            skArc(sketch, "E754.filletArc", {"start": v(19.83, -13.58) * mm, "mid": v(19.86, -13.93) * mm, "end": v(20.04, -14.23) * mm});
            skPoint(sketch, "E755.visualSharp", {"position": v(18.52, -9.7) * mm});
            skArc(sketch, "E755.filletArc", {"start": v(18.86, -9.37) * mm, "mid": v(18.71, -9.7) * mm, "end": v(18.84, -10.06) * mm});
            skPoint(sketch, "E756.visualSharp", {"position": v(27.4, -21.59) * mm});
            skArc(sketch, "E756.filletArc", {"start": v(23.86, -18.04) * mm, "mid": v(25.12, -18.16) * mm, "end": v(25.49, -16.95) * mm});
            skLineSegment(sketch, "E757", {"start": v(-0.01, -29.14) * mm, "end": v(15.24, -29.14) * mm, "construction": true});
            skPoint(sketch, "E758.visualSharp", {"position": v(-9.17, -19.05) * mm});
            skPoint(sketch, "E759.visualSharp", {"position": v(-11.98, -16.25) * mm});
            skPoint(sketch, "E760.visualSharp", {"position": v(-16.23, -17.5) * mm});
            skPoint(sketch, "E761.visualSharp", {"position": v(-23.86, -25.13) * mm});
            skLineSegment(sketch, "E762", {"start": v(15.25, -12.98) * mm, "end": v(9.18, -19.05) * mm, "construction": true});
            skLineSegment(sketch, "E763", {"start": v(11.14, -12.4) * mm, "end": v(23.88, -25.12) * mm, "construction": true});
            skPoint(sketch, "E764", {"position": v(13.76, -17.36) * mm});
            skPoint(sketch, "E765.visualSharp", {"position": v(9.18, -19.05) * mm});
            skPoint(sketch, "E766.visualSharp", {"position": v(11.98, -16.25) * mm});
            skPoint(sketch, "E767.visualSharp", {"position": v(23.88, -25.12) * mm});
            skPoint(sketch, "E768.visualSharp", {"position": v(16.24, -17.5) * mm});
            skPoint(sketch, "E769", {"position": v(-14.29, -17.5) * mm});
            skLineSegment(sketch, "E770", {"start": v(-28.67, 37.26) * mm, "end": v(-26.94, 36.26) * mm, "construction": true});
            skLineSegment(sketch, "E771", {"start": v(28.62, 37.26) * mm, "end": v(26.9, 36.24) * mm, "construction": true});
            skPoint(sketch, "E772", {"position": v(27.69, 36.82) * mm});
            skArc(sketch, "E773", {"start": v(28.62, 37.26) * mm, "mid": v(27.7, 36.84) * mm, "end": v(26.9, 36.24) * mm});
            skPoint(sketch, "E774", {"position": v(-27.73, 36.83) * mm});
            skArc(sketch, "E775", {"start": v(-26.94, 36.26) * mm, "mid": v(-27.76, 36.85) * mm, "end": v(-28.67, 37.26) * mm});
            skLineSegment(sketch, "E776", {"start": v(-26.94, 36.26) * mm, "end": v(-15.28, 26.77) * mm});
            skLineSegment(sketch, "E777", {"start": v(26.9, 36.24) * mm, "end": v(15.22, 26.77) * mm});
            skPoint(sketch, "E778", {"position": v(-0.03, 22) * mm});
            skFitSpline(sketch, "E779", {"points": [v(-15.28, 26.77) * mm, v(-0.03, 22) * mm, v(15.22, 26.77) * mm], "startDerivative": vector(26.4, -17.68) * mm, "endDerivative": vector(26.05, 17.77) * mm});
            skLineSegment(sketch, "E780", {"start": v(10.88, 23.81) * mm, "end": v(0, 23.82) * mm, "construction": true});
            skLineSegment(sketch, "E781", {"start": v(0, 23.82) * mm, "end": v(-10.88, 23.83) * mm, "construction": true});
            skLineSegment(sketch, "E782", {"start": v(-28.65, -32.7) * mm, "end": v(-26.92, -31.7) * mm, "construction": true});
            skLineSegment(sketch, "E783", {"start": v(28.64, -32.72) * mm, "end": v(26.91, -31.71) * mm, "construction": true});
            skPoint(sketch, "E784", {"position": v(27.67, -32.27) * mm});
            skArc(sketch, "E785", {"start": v(26.91, -31.71) * mm, "mid": v(27.73, -32.3) * mm, "end": v(28.64, -32.72) * mm});
            skPoint(sketch, "E786", {"position": v(-27.7, -32.27) * mm});
            skArc(sketch, "E787", {"start": v(-28.65, -32.7) * mm, "mid": v(-27.73, -32.29) * mm, "end": v(-26.92, -31.7) * mm});
            skLineSegment(sketch, "E788", {"start": v(-0.01, -29.14) * mm, "end": v(-15.26, -29.14) * mm, "construction": true});
            skLineSegment(sketch, "E789", {"start": v(-26.92, -31.7) * mm, "end": v(-15.26, -23.98) * mm});
            skLineSegment(sketch, "E790", {"start": v(26.91, -31.71) * mm, "end": v(15.24, -23.98) * mm});
            skLineSegment(sketch, "E791", {"start": v(-0.01, -14.83) * mm, "end": v(-0.01, -17.45) * mm, "construction": true});
            skLineSegment(sketch, "E792", {"start": v(-0.01, -17.45) * mm, "end": v(-0.01, -19.27) * mm, "construction": true});
            skFitSpline(sketch, "E793", {"points": [v(-15.26, -23.98) * mm, v(-0.01, -17.45) * mm, v(15.24, -23.98) * mm], "startDerivative": vector(30.5, 19.6) * mm, "endDerivative": vector(30.5, -19.6) * mm});
            skLineSegment(sketch, "E794", {"start": v(-0.01, -19.27) * mm, "end": v(10.87, -19.27) * mm, "construction": true});
            skLineSegment(sketch, "E795", {"start": v(-0.01, -19.27) * mm, "end": v(-10.9, -19.27) * mm, "construction": true});
            skLineSegment(sketch, "E796", {"start": v(0, -12.98) * mm, "end": v(0, -10.98) * mm, "construction": true});
            skFitSpline(sketch, "E797", {"points": [v(-7.75, -12.98) * mm, v(0, -10.98) * mm, v(7.72, -12.98) * mm], "startDerivative": vector(15.5, 6) * mm, "endDerivative": vector(15.45, -6) * mm});
            skLineSegment(sketch, "E798", {"start": v(-0.03, 17.52) * mm, "end": v(-0.03, 15.52) * mm, "construction": true});
            skFitSpline(sketch, "E799", {"points": [v(-7.75, 17.52) * mm, v(-0.03, 15.52) * mm, v(7.72, 17.52) * mm], "startDerivative": vector(15.45, -6) * mm, "endDerivative": vector(15.5, 6) * mm});
            skSolve(sketch);
        }
        {
            var Q0;
            Q0=qCreatedBy(makeId("Top.planeOp"),FACE);
            var sketch = newSketch(context, id + "F6", { "sketchPlane" : qUnion([Q0])});
            skLineSegment(sketch, "E800.bottom", {"start": v(-15.25, 15.28) * mm, "end": v(15.25, 15.28) * mm, "construction": true});
            skLineSegment(sketch, "E800.top", {"start": v(-15.25, -15.22) * mm, "end": v(15.25, -15.22) * mm, "construction": true});
            skLineSegment(sketch, "E800.left", {"start": v(-15.25, 15.28) * mm, "end": v(-15.25, -15.22) * mm, "construction": true});
            skLineSegment(sketch, "E800.right", {"start": v(15.25, 15.28) * mm, "end": v(15.25, -15.22) * mm, "construction": true});
            skPoint(sketch, "E800.middle", {"position": v(0, 0.03) * mm});
            skLineSegment(sketch, "E801.bottom", {"start": v(30.25, 30.28) * mm, "end": v(-30.25, 30.28) * mm, "construction": true});
            skLineSegment(sketch, "E801.top", {"start": v(30.25, -30.22) * mm, "end": v(-30.25, -30.22) * mm, "construction": true});
            skLineSegment(sketch, "E801.left", {"start": v(30.25, 30.28) * mm, "end": v(30.25, -30.22) * mm, "construction": true});
            skLineSegment(sketch, "E801.right", {"start": v(-30.25, 30.28) * mm, "end": v(-30.25, -30.22) * mm, "construction": true});
            skLineSegment(sketch, "E802.bottom", {"start": v(-70.96, 70.99) * mm, "end": v(70.96, 70.99) * mm, "construction": true});
            skLineSegment(sketch, "E802.top", {"start": v(-70.96, -70.93) * mm, "end": v(70.96, -70.93) * mm, "construction": true});
            skLineSegment(sketch, "E802.left", {"start": v(-70.96, 70.99) * mm, "end": v(-70.96, -70.93) * mm, "construction": true});
            skLineSegment(sketch, "E802.right", {"start": v(70.96, 70.99) * mm, "end": v(70.96, -70.93) * mm, "construction": true});
            skCircle(sketch, "E803", {"center": v(70.96, 70.99) * mm, "radius": 4.5 * mm, "construction": true});
            skCircle(sketch, "E804", {"center": v(-70.96, 70.99) * mm, "radius": 4.5 * mm, "construction": true});
            skCircle(sketch, "E805", {"center": v(70.96, -70.93) * mm, "radius": 4.5 * mm, "construction": true});
            skCircle(sketch, "E806", {"center": v(-70.96, -70.93) * mm, "radius": 4.5 * mm, "construction": true});
            skCircle(sketch, "E807", {"center": v(70.96, 70.99) * mm, "radius": 8 * mm, "construction": true});
            skCircle(sketch, "E808", {"center": v(70.96, -70.93) * mm, "radius": 8 * mm, "construction": true});
            skCircle(sketch, "E809", {"center": v(-70.96, -70.93) * mm, "radius": 8 * mm, "construction": true});
            skCircle(sketch, "E810", {"center": v(-70.96, 70.99) * mm, "radius": 8 * mm, "construction": true});
            skCircle(sketch, "E811", {"center": v(70.96, 70.99) * mm, "radius": 9.5 * mm, "construction": true});
            skCircle(sketch, "E812", {"center": v(70.96, -70.93) * mm, "radius": 9.5 * mm, "construction": true});
            skCircle(sketch, "E813", {"center": v(-70.96, -70.93) * mm, "radius": 9.5 * mm, "construction": true});
            skCircle(sketch, "E814", {"center": v(-70.96, 70.99) * mm, "radius": 9.5 * mm, "construction": true});
            skCircle(sketch, "E815", {"center": v(70.96, 70.99) * mm, "radius": 14 * mm, "construction": true});
            skCircle(sketch, "E816", {"center": v(-70.96, 70.99) * mm, "radius": 14 * mm, "construction": true});
            skCircle(sketch, "E817", {"center": v(70.96, -70.93) * mm, "radius": 14 * mm, "construction": true});
            skCircle(sketch, "E818", {"center": v(-70.96, -70.93) * mm, "radius": 14 * mm, "construction": true});
            skCircle(sketch, "E819", {"center": v(70.96, 70.99) * mm, "radius": 63.5 * mm, "construction": true});
            skCircle(sketch, "E820", {"center": v(70.96, -70.93) * mm, "radius": 63.5 * mm, "construction": true});
            skCircle(sketch, "E821", {"center": v(-70.96, -70.93) * mm, "radius": 63.5 * mm, "construction": true});
            skCircle(sketch, "E822", {"center": v(-70.96, 70.99) * mm, "radius": 63.5 * mm, "construction": true});
            skLineSegment(sketch, "E823", {"start": v(0, 30.28) * mm, "end": v(0, 33.77) * mm, "construction": true});
            skLineSegment(sketch, "E824", {"start": v(0, 33.77) * mm, "end": v(-15, 33.77) * mm, "construction": true});
            skLineSegment(sketch, "E825", {"start": v(0, 33.77) * mm, "end": v(15, 33.77) * mm, "construction": true});
            skLineSegment(sketch, "E826", {"start": v(0, -30.22) * mm, "end": v(0, -33.72) * mm, "construction": true});
            skLineSegment(sketch, "E827", {"start": v(0, -33.72) * mm, "end": v(-15, -33.72) * mm, "construction": true});
            skLineSegment(sketch, "E828", {"start": v(0, -33.72) * mm, "end": v(15, -33.72) * mm, "construction": true});
            skLineSegment(sketch, "E829.bottom", {"start": v(-26.19, 26.22) * mm, "end": v(26.2, 26.22) * mm, "construction": true});
            skLineSegment(sketch, "E829.top", {"start": v(-26.19, -26.16) * mm, "end": v(26.2, -26.16) * mm, "construction": true});
            skLineSegment(sketch, "E829.left", {"start": v(-26.19, 26.22) * mm, "end": v(-26.19, -26.16) * mm, "construction": true});
            skLineSegment(sketch, "E829.right", {"start": v(26.2, 26.22) * mm, "end": v(26.2, -26.16) * mm, "construction": true});
            skCircle(sketch, "E830", {"center": v(30.25, 30.28) * mm, "radius": 3.57 * mm, "construction": true});
            skCircle(sketch, "E831", {"center": v(-30.25, 30.28) * mm, "radius": 3.57 * mm, "construction": true});
            skCircle(sketch, "E832", {"center": v(30.25, -30.22) * mm, "radius": 3.57 * mm, "construction": true});
            skCircle(sketch, "E833", {"center": v(-30.25, -30.22) * mm, "radius": 3.57 * mm, "construction": true});
            skLineSegment(sketch, "E834", {"start": v(-70.96, 70.99) * mm, "end": v(70.96, -70.93) * mm, "construction": true});
            skLineSegment(sketch, "E835", {"start": v(0, -26.16) * mm, "end": v(17.54, -26.16) * mm, "construction": true});
            skLineSegment(sketch, "E836", {"start": v(0, -26.16) * mm, "end": v(-17.54, -26.16) * mm, "construction": true});
            skLineSegment(sketch, "E837", {"start": v(0, -33.72) * mm, "end": v(0, -44.57) * mm, "construction": true});
            skLineSegment(sketch, "E838", {"start": v(0, -44.57) * mm, "end": v(0, -48.1) * mm, "construction": true});
            skLineSegment(sketch, "E839", {"start": v(0, -44.57) * mm, "end": v(11, -44.57) * mm, "construction": true});
            skLineSegment(sketch, "E840", {"start": v(0, -44.57) * mm, "end": v(-11, -44.57) * mm, "construction": true});
            skLineSegment(sketch, "E841", {"start": v(-15.25, -15.22) * mm, "end": v(-19.25, -15.22) * mm, "construction": true});
            skLineSegment(sketch, "E842", {"start": v(15.25, -15.22) * mm, "end": v(19.25, -15.22) * mm, "construction": true});
            skLineSegment(sketch, "E843", {"start": v(15.25, 15.28) * mm, "end": v(19.25, 15.28) * mm, "construction": true});
            skLineSegment(sketch, "E844", {"start": v(-15.25, 15.28) * mm, "end": v(-19.25, 15.28) * mm, "construction": true});
            skLineSegment(sketch, "E845", {"start": v(-16.22, -31.94) * mm, "end": v(0, -31.94) * mm, "construction": true});
            skLineSegment(sketch, "E846", {"start": v(0, -31.94) * mm, "end": v(16.22, -31.94) * mm, "construction": true});
            skLineSegment(sketch, "E847", {"start": v(-12.6, -42.84) * mm, "end": v(0, -42.84) * mm, "construction": true});
            skLineSegment(sketch, "E848", {"start": v(0, -42.84) * mm, "end": v(12.6, -42.84) * mm, "construction": true});
            skFitSpline(sketch, "E849", {"points": [v(-11, -44.57) * mm, v(0, -48.1) * mm], "startDerivative": vector(9.3, -7.23) * mm, "endDerivative": vector(12, -2.3) * mm});
            skFitSpline(sketch, "E850", {"points": [v(11, -44.57) * mm, v(0, -48.1) * mm], "startDerivative": vector(-9.3, -7.23) * mm, "endDerivative": vector(-12, -2.3) * mm});
            skLineSegment(sketch, "E851", {"start": v(-7.9, -46.98) * mm, "end": v(0, -46.98) * mm, "construction": true});
            skLineSegment(sketch, "E852", {"start": v(0, -46.98) * mm, "end": v(7.9, -46.98) * mm, "construction": true});
            skLineSegment(sketch, "E853", {"start": v(-4, -47.35) * mm, "end": v(0, -47.35) * mm, "construction": true});
            skLineSegment(sketch, "E854", {"start": v(0, -47.35) * mm, "end": v(4, -47.35) * mm, "construction": true});
            skCircle(sketch, "E855", {"center": v(-8.33, -41.13) * mm, "radius": 1.5 * mm});
            skCircle(sketch, "E856", {"center": v(8.33, -41.13) * mm, "radius": 1.5 * mm});
            skFitSpline(sketch, "E857", {"points": [v(-15, 33.77) * mm, v(-19.25, 15.28) * mm], "startDerivative": vector(-1.66, -47.23) * mm, "endDerivative": vector(-4.95, -22.5) * mm});
            skFitSpline(sketch, "E858", {"points": [v(15, 33.77) * mm, v(19.25, 15.28) * mm], "startDerivative": vector(1.66, -47.23) * mm, "endDerivative": vector(4.95, -22.5) * mm});
            skLineSegment(sketch, "E859", {"start": v(-19.25, 15.28) * mm, "end": v(-19.25, -15.22) * mm});
            skLineSegment(sketch, "E860", {"start": v(19.25, 15.28) * mm, "end": v(19.25, -15.22) * mm});
            skArc(sketch, "E861.filletArc", {"start": v(-13.08, 33.76) * mm, "mid": v(-14.46, 33.21) * mm, "end": v(-15.08, 31.86) * mm});
            skArc(sketch, "E862.filletArc", {"start": v(15.08, 31.86) * mm, "mid": v(14.46, 33.21) * mm, "end": v(13.08, 33.76) * mm});
            skLineSegment(sketch, "E863", {"start": v(15.55, 18.03) * mm, "end": v(0, 18.03) * mm, "construction": true});
            skLineSegment(sketch, "E864", {"start": v(0, 18.03) * mm, "end": v(-15.55, 18.03) * mm, "construction": true});
            skPoint(sketch, "E865.visualSharp", {"position": v(-17.54, -26.16) * mm});
            skPoint(sketch, "E866.visualSharp", {"position": v(17.54, -26.16) * mm});
            skFitSpline(sketch, "E867", {"points": [v(-19.25, -15.22) * mm, v(-17.54, -26.16) * mm, v(-12.6, -42.84) * mm, v(-11, -44.57) * mm], "startDerivative": vector(1.48, -36.7) * mm, "endDerivative": vector(10.67, -6.67) * mm});
            skFitSpline(sketch, "E868", {"points": [v(19.25, -15.22) * mm, v(17.54, -26.16) * mm, v(12.6, -42.84) * mm, v(11, -44.57) * mm], "startDerivative": vector(-1.5, -36.7) * mm, "endDerivative": vector(-10.67, -6.67) * mm});
            skLineSegment(sketch, "E869", {"start": v(-8.33, -41.13) * mm, "end": v(-13.33, -41.13) * mm, "construction": true});
            skLineSegment(sketch, "E870", {"start": v(-8.33, -41.13) * mm, "end": v(-8.33, -46.13) * mm, "construction": true});
            skLineSegment(sketch, "E871", {"start": v(8.33, -41.13) * mm, "end": v(13.33, -41.13) * mm, "construction": true});
            skLineSegment(sketch, "E872", {"start": v(8.33, -41.13) * mm, "end": v(8.33, -46.13) * mm, "construction": true});
            skLineSegment(sketch, "E873", {"start": v(-11.5, 33.76) * mm, "end": v(-11.5, 29.76) * mm, "construction": true});
            skLineSegment(sketch, "E874", {"start": v(-11.5, 29.76) * mm, "end": v(-15.2, 29.76) * mm, "construction": true});
            skLineSegment(sketch, "E875", {"start": v(11.5, 33.76) * mm, "end": v(11.5, 29.76) * mm, "construction": true});
            skLineSegment(sketch, "E876", {"start": v(11.5, 29.76) * mm, "end": v(15.2, 29.76) * mm, "construction": true});
            skCircle(sketch, "E877", {"center": v(-11.5, 29.76) * mm, "radius": 1.5 * mm});
            skCircle(sketch, "E878", {"center": v(11.5, 29.76) * mm, "radius": 1.5 * mm});
            skCircle(sketch, "E879", {"center": v(-15.25, 15.28) * mm, "radius": 1.5 * mm});
            skCircle(sketch, "E880", {"center": v(15.25, 15.28) * mm, "radius": 1.5 * mm});
            skCircle(sketch, "E881", {"center": v(15.25, -15.22) * mm, "radius": 1.5 * mm});
            skCircle(sketch, "E882", {"center": v(-15.25, -15.22) * mm, "radius": 1.5 * mm});
            skLineSegment(sketch, "E883.bottom", {"start": v(-13.67, 13.7) * mm, "end": v(13.68, 13.7) * mm, "construction": true});
            skLineSegment(sketch, "E883.top", {"start": v(-13.67, -13.65) * mm, "end": v(13.68, -13.65) * mm, "construction": true});
            skLineSegment(sketch, "E883.left", {"start": v(-13.68, 13.7) * mm, "end": v(-13.68, -13.65) * mm, "construction": true});
            skLineSegment(sketch, "E883.right", {"start": v(13.67, 13.7) * mm, "end": v(13.67, -13.65) * mm, "construction": true});
            skLineSegment(sketch, "E884.bottom", {"start": v(-4.75, 4.78) * mm, "end": v(4.75, 4.78) * mm, "construction": true});
            skLineSegment(sketch, "E884.top", {"start": v(-4.75, -4.72) * mm, "end": v(4.75, -4.72) * mm, "construction": true});
            skLineSegment(sketch, "E884.left", {"start": v(-4.75, 4.78) * mm, "end": v(-4.75, -4.72) * mm, "construction": true});
            skLineSegment(sketch, "E884.right", {"start": v(4.75, 4.78) * mm, "end": v(4.75, -4.72) * mm, "construction": true});
            skPoint(sketch, "E885", {"position": v(-4.75, 0.03) * mm});
            skPoint(sketch, "E886", {"position": v(0, 4.78) * mm});
            skPoint(sketch, "E887", {"position": v(4.75, 0.03) * mm});
            skPoint(sketch, "E888", {"position": v(0, -4.72) * mm});
            skLineSegment(sketch, "E889", {"start": v(-6.16, 1.44) * mm, "end": v(-11.97, 7.25) * mm});
            skLineSegment(sketch, "E890", {"start": v(-6.16, -1.39) * mm, "end": v(-11.97, -7.19) * mm});
            skLineSegment(sketch, "E891", {"start": v(-13.68, -6.48) * mm, "end": v(-13.68, 6.54) * mm});
            skLineSegment(sketch, "E892", {"start": v(6.16, -1.39) * mm, "end": v(11.97, -7.19) * mm});
            skLineSegment(sketch, "E893", {"start": v(6.16, 1.44) * mm, "end": v(11.97, 7.25) * mm});
            skLineSegment(sketch, "E894", {"start": v(13.67, 6.54) * mm, "end": v(13.67, -6.48) * mm});
            skArc(sketch, "E895.filletArc", {"start": v(-6.16, -1.39) * mm, "mid": v(-5.58, 0.03) * mm, "end": v(-6.16, 1.44) * mm});
            skPoint(sketch, "E896.visualSharp", {"position": v(-13.67, 8.95) * mm});
            skArc(sketch, "E896.filletArc", {"start": v(-11.97, 7.25) * mm, "mid": v(-13.06, 7.46) * mm, "end": v(-13.67, 6.54) * mm});
            skPoint(sketch, "E897.visualSharp", {"position": v(-13.67, -8.9) * mm});
            skArc(sketch, "E897.filletArc", {"start": v(-13.67, -6.48) * mm, "mid": v(-13.06, -7.4) * mm, "end": v(-11.97, -7.19) * mm});
            skArc(sketch, "E898.filletArc", {"start": v(6.16, 1.44) * mm, "mid": v(5.58, 0.03) * mm, "end": v(6.16, -1.39) * mm});
            skPoint(sketch, "E899.visualSharp", {"position": v(13.68, 8.95) * mm});
            skArc(sketch, "E899.filletArc", {"start": v(13.68, 6.54) * mm, "mid": v(13.06, 7.46) * mm, "end": v(11.97, 7.25) * mm});
            skPoint(sketch, "E900.visualSharp", {"position": v(13.68, -8.9) * mm});
            skArc(sketch, "E900.filletArc", {"start": v(11.97, -7.19) * mm, "mid": v(13.06, -7.4) * mm, "end": v(13.68, -6.48) * mm});
            skLineSegment(sketch, "E901", {"start": v(1.41, -6.14) * mm, "end": v(7.22, -11.94) * mm});
            skLineSegment(sketch, "E902", {"start": v(-1.41, -6.14) * mm, "end": v(-7.22, -11.94) * mm});
            skLineSegment(sketch, "E903", {"start": v(-6.51, -13.65) * mm, "end": v(6.51, -13.65) * mm});
            skArc(sketch, "E904.filletArc", {"start": v(1.41, -6.14) * mm, "mid": v(0, -5.55) * mm, "end": v(-1.41, -6.14) * mm});
            skPoint(sketch, "E905.visualSharp", {"position": v(8.92, -13.65) * mm});
            skArc(sketch, "E905.filletArc", {"start": v(6.51, -13.65) * mm, "mid": v(7.43, -13.03) * mm, "end": v(7.22, -11.94) * mm});
            skPoint(sketch, "E906.visualSharp", {"position": v(-8.93, -13.65) * mm});
            skArc(sketch, "E906.filletArc", {"start": v(-7.22, -11.94) * mm, "mid": v(-7.43, -13.03) * mm, "end": v(-6.51, -13.65) * mm});
            skLineSegment(sketch, "E907", {"start": v(0, -17.8) * mm, "end": v(13.36, -17.8) * mm, "construction": true});
            skPoint(sketch, "E908", {"position": v(0, -17.8) * mm});
            skLineSegment(sketch, "E909", {"start": v(0, -17.8) * mm, "end": v(-13.36, -17.8) * mm, "construction": true});
            skLineSegment(sketch, "E910", {"start": v(-8.92, -13.65) * mm, "end": v(-8.92, -17.8) * mm, "construction": true});
            skLineSegment(sketch, "E911", {"start": v(8.92, -13.65) * mm, "end": v(8.92, -17.8) * mm, "construction": true});
            skLineSegment(sketch, "E912", {"start": v(0, -17.8) * mm, "end": v(0, -26.72) * mm, "construction": true});
            skLineSegment(sketch, "E913", {"start": v(-7.22, -19.5) * mm, "end": v(-1.41, -25.3) * mm});
            skLineSegment(sketch, "E914", {"start": v(1.41, -25.3) * mm, "end": v(7.22, -19.5) * mm});
            skLineSegment(sketch, "E915", {"start": v(6.51, -17.8) * mm, "end": v(-6.51, -17.8) * mm});
            skPoint(sketch, "E916.visualSharp", {"position": v(-8.92, -17.8) * mm});
            skArc(sketch, "E916.filletArc", {"start": v(-6.51, -17.8) * mm, "mid": v(-7.43, -18.42) * mm, "end": v(-7.22, -19.5) * mm});
            skPoint(sketch, "E917.visualSharp", {"position": v(8.92, -17.8) * mm});
            skArc(sketch, "E917.filletArc", {"start": v(7.22, -19.5) * mm, "mid": v(7.43, -18.42) * mm, "end": v(6.51, -17.8) * mm});
            skPoint(sketch, "E918.visualSharp", {"position": v(0, -26.72) * mm});
            skArc(sketch, "E918.filletArc", {"start": v(-1.41, -25.3) * mm, "mid": v(0, -25.9) * mm, "end": v(1.41, -25.3) * mm});
            skLineSegment(sketch, "E919", {"start": v(0, -21.22) * mm, "end": v(-11.7, -21.22) * mm, "construction": true});
            skLineSegment(sketch, "E920", {"start": v(0, -21.22) * mm, "end": v(11.7, -21.22) * mm, "construction": true});
            skLineSegment(sketch, "E921", {"start": v(-10.43, -22.48) * mm, "end": v(-4.5, -28.4) * mm});
            skLineSegment(sketch, "E922", {"start": v(-3.92, -29.82) * mm, "end": v(-3.92, -33) * mm});
            skLineSegment(sketch, "E923", {"start": v(-11.27, -22.95) * mm, "end": v(-9.07, -31.94) * mm});
            skArc(sketch, "E924", {"start": v(-9.07, -31.94) * mm, "mid": v(-6.94, -34.19) * mm, "end": v(-3.92, -33.5) * mm, "construction": true});
            skLineSegment(sketch, "E925", {"start": v(-4.32, -33.8) * mm, "end": v(-4.4, -33.86) * mm});
            skPoint(sketch, "E926", {"position": v(-6.94, -34.19) * mm});
            skArc(sketch, "E927", {"start": v(-9.07, -31.94) * mm, "mid": v(-7.22, -34.09) * mm, "end": v(-4.4, -33.86) * mm});
            skPoint(sketch, "E928.visualSharp", {"position": v(-11.7, -21.22) * mm});
            skArc(sketch, "E928.filletArc", {"start": v(-10.43, -22.48) * mm, "mid": v(-11.03, -22.4) * mm, "end": v(-11.27, -22.95) * mm});
            skPoint(sketch, "E929.visualSharp", {"position": v(-3.92, -29) * mm});
            skArc(sketch, "E929.filletArc", {"start": v(-3.92, -29.82) * mm, "mid": v(-4.07, -29.06) * mm, "end": v(-4.5, -28.4) * mm});
            skPoint(sketch, "E930.visualSharp", {"position": v(-3.92, -33.5) * mm});
            skArc(sketch, "E930.filletArc", {"start": v(-4.32, -33.8) * mm, "mid": v(-4.03, -33.44) * mm, "end": v(-3.92, -33) * mm});
            skLineSegment(sketch, "E931", {"start": v(10.43, -22.48) * mm, "end": v(4.5, -28.4) * mm});
            skLineSegment(sketch, "E932", {"start": v(3.92, -29.82) * mm, "end": v(3.92, -33) * mm});
            skLineSegment(sketch, "E933", {"start": v(3.92, -31.94) * mm, "end": v(9.07, -31.94) * mm, "construction": true});
            skArc(sketch, "E934", {"start": v(3.92, -33.5) * mm, "mid": v(6.94, -34.19) * mm, "end": v(9.07, -31.94) * mm, "construction": true});
            skLineSegment(sketch, "E935", {"start": v(11.27, -22.95) * mm, "end": v(9.07, -31.94) * mm});
            skLineSegment(sketch, "E936", {"start": v(4.32, -33.8) * mm, "end": v(4.4, -33.86) * mm});
            skPoint(sketch, "E937", {"position": v(6.94, -34.19) * mm});
            skArc(sketch, "E938", {"start": v(4.4, -33.86) * mm, "mid": v(7.22, -34.09) * mm, "end": v(9.07, -31.94) * mm});
            skPoint(sketch, "E939.visualSharp", {"position": v(3.92, -29) * mm});
            skArc(sketch, "E939.filletArc", {"start": v(4.5, -28.4) * mm, "mid": v(4.07, -29.06) * mm, "end": v(3.92, -29.82) * mm});
            skPoint(sketch, "E940.visualSharp", {"position": v(3.92, -33.5) * mm});
            skArc(sketch, "E940.filletArc", {"start": v(3.92, -33) * mm, "mid": v(4.03, -33.44) * mm, "end": v(4.32, -33.8) * mm});
            skPoint(sketch, "E941.visualSharp", {"position": v(11.7, -21.22) * mm});
            skArc(sketch, "E941.filletArc", {"start": v(11.27, -22.95) * mm, "mid": v(11.03, -22.4) * mm, "end": v(10.43, -22.48) * mm});
            skLineSegment(sketch, "E942", {"start": v(-8.92, -13.65) * mm, "end": v(-8.92, 13.7) * mm, "construction": true});
            skLineSegment(sketch, "E943", {"start": v(8.92, -13.65) * mm, "end": v(8.92, 13.7) * mm, "construction": true});
            skLineSegment(sketch, "E944", {"start": v(-1.41, 6.2) * mm, "end": v(-7.22, 12) * mm});
            skLineSegment(sketch, "E945", {"start": v(1.41, 6.2) * mm, "end": v(7.22, 12) * mm});
            skLineSegment(sketch, "E946", {"start": v(6.51, 13.7) * mm, "end": v(-6.51, 13.7) * mm});
            skArc(sketch, "E947.filletArc", {"start": v(-1.41, 6.2) * mm, "mid": v(0, 5.6) * mm, "end": v(1.41, 6.2) * mm});
            skPoint(sketch, "E948.visualSharp", {"position": v(8.92, 13.7) * mm});
            skArc(sketch, "E948.filletArc", {"start": v(7.22, 12) * mm, "mid": v(7.43, 13.09) * mm, "end": v(6.51, 13.7) * mm});
            skPoint(sketch, "E949.visualSharp", {"position": v(-8.93, 13.7) * mm});
            skArc(sketch, "E949.filletArc", {"start": v(-6.51, 13.7) * mm, "mid": v(-7.43, 13.09) * mm, "end": v(-7.22, 12) * mm});
            skLineSegment(sketch, "E950", {"start": v(0, 32.03) * mm, "end": v(8.5, 32.03) * mm, "construction": true});
            skPoint(sketch, "E950.endSnap0", {"position": v(0, 32.03) * mm});
            skLineSegment(sketch, "E951", {"start": v(0, 32.03) * mm, "end": v(-8.5, 32.03) * mm, "construction": true});
            skFitSpline(sketch, "E952", {"points": [v(-8.5, 32.03) * mm, v(-8.5, 33.77) * mm], "startDerivative": vector(0, 1.74) * mm, "endDerivative": vector(0, 1.74) * mm});
            skFitSpline(sketch, "E953", {"points": [v(8.5, 32.03) * mm, v(8.5, 33.77) * mm], "startDerivative": vector(0, 1.74) * mm, "endDerivative": vector(0, 1.74) * mm});
            skLineSegment(sketch, "E954", {"start": v(-9.5, 33.77) * mm, "end": v(-13.08, 33.76) * mm});
            skFitSpline(sketch, "E955", {"points": [v(8.5, 33.77) * mm, v(13.08, 33.76) * mm], "startDerivative": vector(4.35, 0) * mm, "endDerivative": vector(4.35, 0) * mm});
            skArc(sketch, "E956.filletArc", {"start": v(9.5, 33.77) * mm, "mid": v(8.8, 33.48) * mm, "end": v(8.5, 32.77) * mm});
            skArc(sketch, "E957.filletArc", {"start": v(-8.5, 32.77) * mm, "mid": v(-8.8, 33.48) * mm, "end": v(-9.5, 33.77) * mm});
            skLineSegment(sketch, "E958", {"start": v(-8.5, 32.29) * mm, "end": v(-8.5, 26.6) * mm});
            skLineSegment(sketch, "E959", {"start": v(8.5, 32.29) * mm, "end": v(8.5, 26.6) * mm});
            skFitSpline(sketch, "E960", {"points": [v(-8.5, 24.54) * mm, v(0, 22.26) * mm, v(8.5, 24.54) * mm], "startDerivative": vector(17.46, -6.82) * mm, "endDerivative": vector(17.46, 6.82) * mm});
            skArc(sketch, "E961.filletArc", {"start": v(-8.5, 26.6) * mm, "mid": v(-7.97, 24.88) * mm, "end": v(-6.56, 23.78) * mm});
            skArc(sketch, "E962.filletArc", {"start": v(6.56, 23.78) * mm, "mid": v(7.97, 24.88) * mm, "end": v(8.5, 26.6) * mm});
            skSolve(sketch);
        }
        {
            var Q0;
            Q0 = qSketchRegion(id + "F6", true);
            extrude(context, id + "F7", {"entities" : qUnion([Q0]), "depth" : 21.5 * mm, "hasSecondDirection" : true, "secondDirectionOppositeDirection" : false, "secondDirectionDepth" : 20 * mm});
        }
        {
            var Q0;
            Q0 = qSketchRegion(id + "F5", true);
            extrude(context, id + "F8", {"entities" : qUnion([Q0]), "depth" : 10.5 * mm, "hasSecondDirection" : true, "secondDirectionOppositeDirection" : false, "secondDirectionDepth" : 9 * mm});
        }
    });
